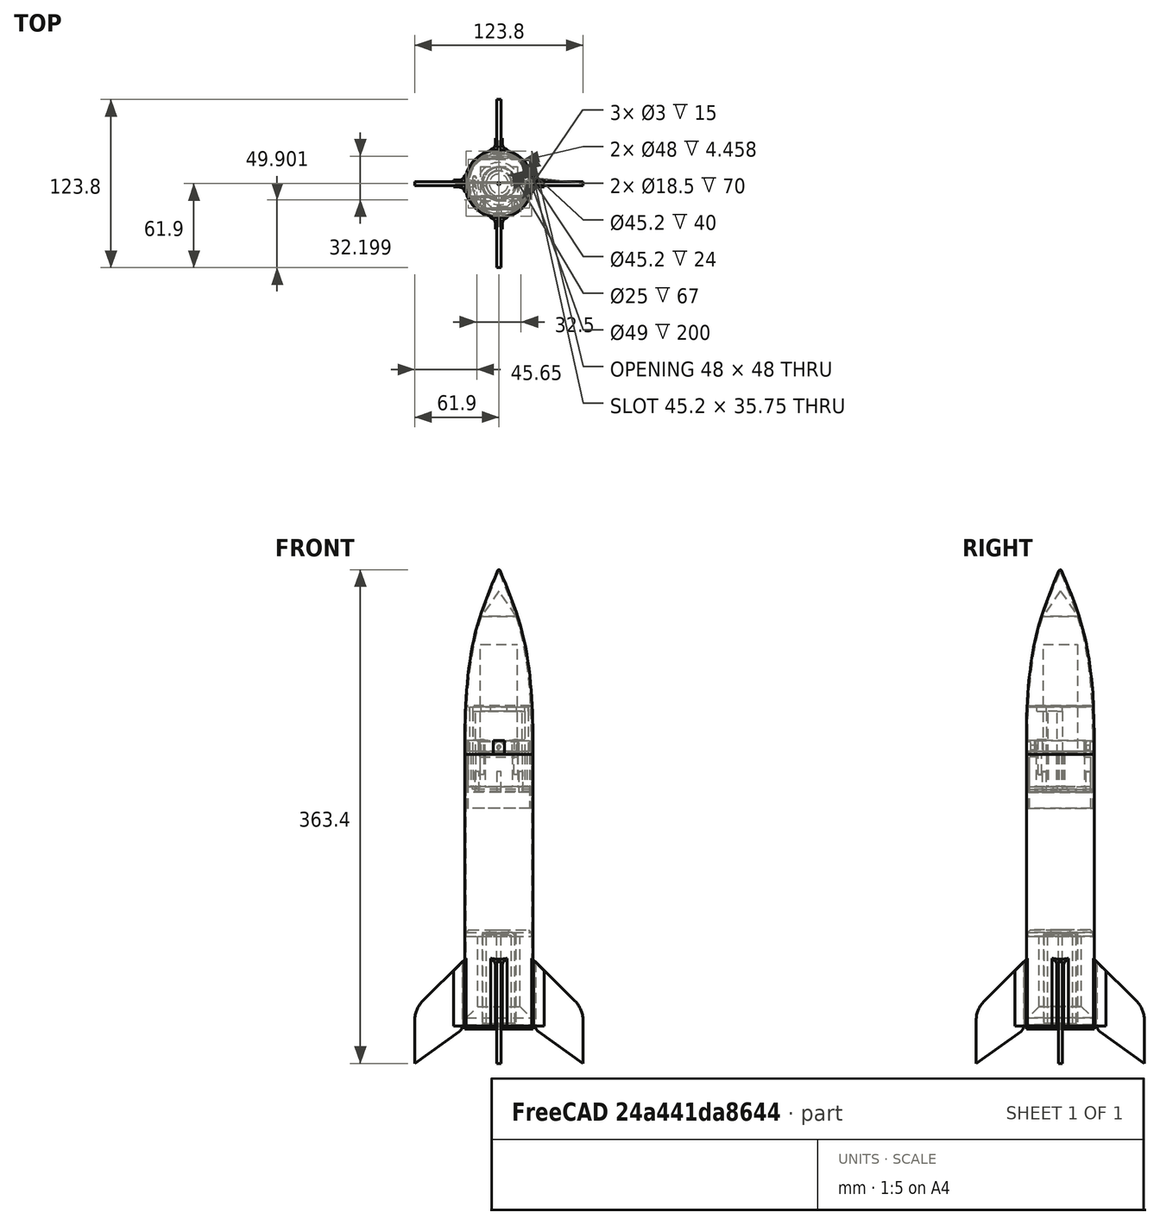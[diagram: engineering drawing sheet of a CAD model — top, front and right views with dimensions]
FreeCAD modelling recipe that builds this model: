
FCSTD DOCUMENT  (FreeCAD 0.21R33694 (Git))
Label: LaMule_V1.2
License: All rights reserved
LicenseURL: http://en.wikipedia.org/wiki/All_rights_reserved
objects: Sketcher::SketchObject×52, PartDesign::Pad×29, PartDesign::Body×19, PartDesign::Pocket×19, PartDesign::Fillet×12, PartDesign::Chamfer×11, Mesh::Feature×5, PartDesign::Revolution×4, App::LinkGroup×2, PartDesign::Thickness×2, TechDraw::DrawSVGTemplate×1, TechDraw::DrawViewPart×1, TechDraw::DrawPage×1
note: 225 computed .brp shape members not serialized (recipe doc carries the construction recipe); baked Part::Feature solids carry a one-line shape summary decoded from their .brp

FEATURE [Sketcher::SketchObject] Sketch
  FullyConstrained = true
  MapMode = 5
  Placement = pos=(0,0,0) rot=(1,0,0;1.5708rad)
  Support = -> [XZ_Plane]
  sketch-geometry (12):
    g0: LineSegment StartX=24 StartY=0 StartZ=0 EndX=7 EndY=0 EndZ=0
    g1: LineSegment StartX=7 StartY=0 StartZ=0 EndX=7 EndY=3 EndZ=0
    g2: LineSegment StartX=7 StartY=3 StartZ=0 EndX=12.5 EndY=3 EndZ=0
    g3: LineSegment StartX=12.5 StartY=3 StartZ=0 EndX=12.5 EndY=73 EndZ=0
    g4: LineSegment StartX=12.5 StartY=73 StartZ=0 EndX=25 EndY=73 EndZ=0
    g5: LineSegment StartX=25 StartY=73 StartZ=0 EndX=25 EndY=71 EndZ=0
    g6: LineSegment StartX=25 StartY=71 StartZ=0 EndX=24 EndY=70 EndZ=0
    g7: LineSegment StartX=24 StartY=70 StartZ=0 EndX=24 EndY=65 EndZ=0
    g8: LineSegment StartX=24 StartY=65 StartZ=0 EndX=15.5 EndY=56.5 EndZ=0
    g9: LineSegment StartX=15.5 StartY=56.5 StartZ=0 EndX=15.5 EndY=5 EndZ=0
    g10: LineSegment StartX=15.5 StartY=5 StartZ=0 EndX=24 EndY=5 EndZ=0
    g11: LineSegment StartX=24 StartY=5 StartZ=0 EndX=24 EndY=0 EndZ=0
  constraints (36):
    c: PointOnObject(g0,g-1)
    c: PointOnObject(g0,g-1)
    c: Coincident(g0,g1)
    c: Vertical(g1)
    c: Coincident(g1,g2)
    c: Horizontal(g2)
    c: Coincident(g2,g3)
    c: Vertical(g3)
    c: Coincident(g3,g4)
    c: Horizontal(g4)
    c: Coincident(g4,g5)
    c: Coincident(g5,g6)
    c: Coincident(g6,g7)
    c: Vertical(g7)
    c: Coincident(g7,g8)
    c: Coincident(g8,g9)
    c: Vertical(g9)
    c: Coincident(g9,g10)
    c: Horizontal(g10)
    c: Coincident(g10,g11)
    c: Coincident(g11,g0)
    c: DistanceX(g-2,g2) = 12.5
    c: DistanceY(g3,g3) = 70
    c: DistanceY(g1,g1) = 3
    c: DistanceX(g-2,g4) = 25
    c: Vertical(g5)
    c: DistanceY(g5,g5) = 2
    c: DistanceY(g7,g7) = 5
    c: DistanceX(g-1,g0) = 24
    c: DistanceX(g-2,g7) = 24
    c: Distance(g9,g3) = 3
    c: DistanceY(g11,g11) = 5
    c: Angle(g9,g8) = 2.35619
    c: Angle(g7,g6) = 2.35619
    c: Vertical(g11)
    c: DistanceX(g-2,g0) = 7
FEATURE [PartDesign::Revolution] Revolution
  Angle = 360
  Axis = (0,2e-16,1)
  Base = (0,0,0)
  Placement = pos=(0,0,0) rot=(1,0,0;1.5708rad)
  Profile = -> Sketch
  ReferenceAxis = -> Sketch [V_Axis]
  Reversed = true
FEATURE [PartDesign::Chamfer] Chamfer
  Angle = 45
  Base = -> Revolution [Edge6]
  BaseFeature = -> Revolution
  ChamferType = 0
  FlipDirection = false
  Placement = pos=(0,0,0) rot=(1,0,0;1.5708rad)
  Size = 3
  Size2 = 1
  SupportTransform = false
  UseAllEdges = false
FEATURE [PartDesign::Chamfer] Chamfer001
  Angle = 45
  Base = -> Chamfer [Edge12]
  BaseFeature = -> Chamfer
  ChamferType = 0
  FlipDirection = false
  Placement = pos=(0,0,0) rot=(1,0,0;1.5708rad)
  Size = 2
  Size2 = 1
  SupportTransform = false
  UseAllEdges = false
FEATURE [PartDesign::Body] Body  label="support_moteur_V1"
  Group = -> [Sketch,Revolution,Chamfer,Chamfer001]
  Origin = -> Origin
  Placement = pos=(7e-15,0,71) rot=(0,1,0;3.14159rad)
  Tip = -> Chamfer001
FEATURE [Sketcher::SketchObject] Sketch001
  FullyConstrained = true
  MapMode = 5
  Support = -> [XY_Plane001]
  sketch-geometry (2):
    g0: Circle CenterX=0 CenterY=0 CenterZ=0 NormalX=0 NormalY=0 NormalZ=1 AngleXU=0 Radius=24.5
    g1: Circle CenterX=0 CenterY=0 CenterZ=0 NormalX=0 NormalY=0 NormalZ=1 AngleXU=0 Radius=25
  constraints (4):
    c: Radius(g0) = 24.5
    c: Radius(g1) = 25
    c: Coincident(g0,g-1)
    c: Coincident(g1,g0)
FEATURE [PartDesign::Pad] Pad
  Direction = (1,1,1)
  Length = 200
  Length2 = 100
  Profile = -> Sketch001
  Type = 0
FEATURE [PartDesign::Body] Body001  label="tube_V1"
  Group = -> [Sketch001,Pad]
  Origin = -> Origin001
  Tip = -> Pad
FEATURE [Sketcher::SketchObject] Sketch002
  FullyConstrained = true
  MapMode = 5
  Support = -> [XY_Plane002]
  sketch-geometry (12):
    g0: ArcOfCircle CenterX=0 CenterY=0 CenterZ=0 NormalX=0 NormalY=0 NormalZ=1 AngleXU=0 Radius=25 StartAngle=6.04082 EndAngle=6.52555
    g1: LineSegment StartX=24.2693 StartY=-6 StartZ=0 EndX=25.2982 EndY=-6 EndZ=0
    g2: LineSegment StartX=24.2693 StartY=6 StartZ=0 EndX=25.2982 EndY=6 EndZ=0
    g3: LineSegment StartX=25.8697 StartY=2.6 StartZ=0 EndX=33.4517 EndY=2.6 EndZ=0
    g4: LineSegment StartX=33.4517 StartY=2.6 StartZ=0 EndX=33.4517 EndY=1.6 EndZ=0
    g5: LineSegment StartX=33.4517 StartY=1.6 StartZ=0 EndX=26.4517 EndY=1.6 EndZ=0
    g6: LineSegment StartX=26.4517 StartY=1.6 StartZ=0 EndX=26.4517 EndY=-1.6 EndZ=0
    g7: LineSegment StartX=26.4517 StartY=-1.6 StartZ=0 EndX=33.4517 EndY=-1.6 EndZ=0
    g8: LineSegment StartX=33.4517 StartY=-1.6 StartZ=0 EndX=33.4517 EndY=-2.6 EndZ=0
    g9: LineSegment StartX=33.4517 StartY=-2.6 StartZ=0 EndX=25.8697 EndY=-2.6 EndZ=0
    g10: ArcOfCircle CenterX=0 CenterY=0 CenterZ=0 NormalX=0 NormalY=0 NormalZ=1 AngleXU=0 Radius=26 StartAngle=6.05032 EndAngle=6.18302
    g11: ArcOfCircle CenterX=0 CenterY=0 CenterZ=0 NormalX=0 NormalY=0 NormalZ=1 AngleXU=0 Radius=26 StartAngle=0.100167 EndAngle=0.232868
  constraints (33):
    c: Coincident(g0,g-1)
    c: Radius(g0) = 25
    c: Coincident(g0,g1)
    c: Coincident(g0,g2)
    c: Horizontal(g3)
    c: Coincident(g3,g4)
    c: Coincident(g4,g5)
    c: Horizontal(g5)
    c: Coincident(g5,g6)
    c: Coincident(g6,g7)
    c: Horizontal(g7)
    c: Coincident(g7,g8)
    c: Coincident(g8,g9)
    c: Horizontal(g9)
    c: Coincident(g10,g0)
    c: Coincident(g10,g1)
    c: Coincident(g10,g9)
    c: Coincident(g11,g0)
    c: Coincident(g11,g2)
    c: Coincident(g11,g3)
    c: Radius(g11) = 26
    c: Horizontal(g2)
    c: Horizontal(g1)
    c: Symmetric(g7,g4,g-1)
    c: Vertical(g8)
    c: Vertical(g6)
    c: Distance(g6,g5) = 3.2
    c: DistanceY(g4,g4) = 1
    c: Distance(g5,g0) = 26.5
    c: Symmetric(g3,g8,g-1)
    c: DistanceX(g5,g5) = 7
    c: Symmetric(g2,g1,g-1)
    c: DistanceY(g-1,g2) = 6
FEATURE [PartDesign::Pad] Pad001
  Direction = (1,1,1)
  Length = 50
  Length2 = 100
  Profile = -> Sketch002
  Type = 0
FEATURE [PartDesign::Fillet] Fillet
  Base = -> Pad001 [Edge20,Edge1]
  BaseFeature = -> Pad001
  Radius = 4
  SupportTransform = false
  UseAllEdges = false
FEATURE [Sketcher::SketchObject] Sketch003
  ExternalGeometry = -> [Fillet]
  FullyConstrained = true
  MapMode = 5
  Placement = pos=(0,-2.6,0) rot=(1,0,0;1.5708rad)
  Support = -> [Fillet]
  sketch-geometry (3):
    g0: LineSegment StartX=33.4517 StartY=50 StartZ=0 EndX=33.4517 EndY=40.8177 EndZ=0
    g1: LineSegment StartX=33.4517 StartY=40.8177 StartZ=0 EndX=24.2693 EndY=50 EndZ=0
    g2: LineSegment StartX=24.2693 StartY=50 StartZ=0 EndX=33.4517 EndY=50 EndZ=0
  constraints (8):
    c: Coincident(g-4,g0)
    c: PointOnObject(g0,g-4)
    c: Coincident(g0,g1)
    c: PointOnObject(g1,g-3)
    c: Coincident(g1,g2)
    c: Coincident(g2,g0)
    c: Horizontal(g2)
    c: Angle(g1,g2) = 0.785398
FEATURE [PartDesign::Pocket] Pocket
  BaseFeature = -> Fillet
  Direction = (1,1,1)
  Length = 23
  Length2 = 100
  Midplane = true
  Profile = -> Sketch003
  Type = 1
FEATURE [PartDesign::Body] Body002  label="support_aileron_V1"
  Group = -> [Sketch002,Pad001,Fillet,Sketch003,Pocket]
  Origin = -> Origin002
  Tip = -> Pocket
FEATURE [Sketcher::SketchObject] Sketch004
  FullyConstrained = true
  MapMode = 5
  Support = -> [XY_Plane003]
  sketch-geometry (12):
    g0: ArcOfCircle CenterX=0 CenterY=0 CenterZ=0 NormalX=0 NormalY=0 NormalZ=1 AngleXU=0 Radius=25 StartAngle=6.04082 EndAngle=6.52555
    g1: LineSegment StartX=24.2693 StartY=-6 StartZ=0 EndX=25.2982 EndY=-6 EndZ=0
    g2: LineSegment StartX=24.2693 StartY=6 StartZ=0 EndX=25.2982 EndY=6 EndZ=0
    g3: LineSegment StartX=25.8697 StartY=2.6 StartZ=0 EndX=33.4517 EndY=2.6 EndZ=0
    g4: LineSegment StartX=33.4517 StartY=2.6 StartZ=0 EndX=33.4517 EndY=1.6 EndZ=0
    g5: LineSegment StartX=33.4517 StartY=1.6 StartZ=0 EndX=26.4517 EndY=1.6 EndZ=0
    g6: LineSegment StartX=26.4517 StartY=1.6 StartZ=0 EndX=26.4517 EndY=-1.6 EndZ=0
    g7: LineSegment StartX=26.4517 StartY=-1.6 StartZ=0 EndX=33.4517 EndY=-1.6 EndZ=0
    g8: LineSegment StartX=33.4517 StartY=-1.6 StartZ=0 EndX=33.4517 EndY=-2.6 EndZ=0
    g9: LineSegment StartX=33.4517 StartY=-2.6 StartZ=0 EndX=25.8697 EndY=-2.6 EndZ=0
    g10: ArcOfCircle CenterX=0 CenterY=0 CenterZ=0 NormalX=0 NormalY=0 NormalZ=1 AngleXU=0 Radius=26 StartAngle=6.05032 EndAngle=6.18302
    g11: ArcOfCircle CenterX=0 CenterY=0 CenterZ=0 NormalX=0 NormalY=0 NormalZ=1 AngleXU=0 Radius=26 StartAngle=0.100167 EndAngle=0.232868
  constraints (33):
    c: Coincident(g0,g-1)
    c: Radius(g0) = 25
    c: Coincident(g0,g1)
    c: Coincident(g0,g2)
    c: Horizontal(g3)
    c: Coincident(g3,g4)
    c: Coincident(g4,g5)
    c: Horizontal(g5)
    c: Coincident(g5,g6)
    c: Coincident(g6,g7)
    c: Horizontal(g7)
    c: Coincident(g7,g8)
    c: Coincident(g8,g9)
    c: Horizontal(g9)
    c: Coincident(g10,g0)
    c: Coincident(g10,g1)
    c: Coincident(g10,g9)
    c: Coincident(g11,g0)
    c: Coincident(g11,g2)
    c: Coincident(g11,g3)
    c: Radius(g11) = 26
    c: Horizontal(g2)
    c: Horizontal(g1)
    c: Symmetric(g7,g4,g-1)
    c: Vertical(g8)
    c: Vertical(g6)
    c: Distance(g6,g5) = 3.2
    c: DistanceY(g4,g4) = 1
    c: Distance(g5,g0) = 26.5
    c: Symmetric(g3,g8,g-1)
    c: DistanceX(g5,g5) = 7
    c: Symmetric(g2,g1,g-1)
    c: DistanceY(g-1,g2) = 6
FEATURE [PartDesign::Pad] Pad002
  Direction = (1,1,1)
  Length = 50
  Length2 = 100
  Profile = -> Sketch004
  Type = 0
FEATURE [PartDesign::Fillet] Fillet001
  Base = -> Pad002 [Edge20,Edge1]
  BaseFeature = -> Pad002
  Radius = 4
  SupportTransform = false
  UseAllEdges = false
FEATURE [Sketcher::SketchObject] Sketch005
  ExternalGeometry = -> [Fillet001]
  FullyConstrained = true
  MapMode = 5
  Placement = pos=(0,-2.6,0) rot=(1,0,0;1.5708rad)
  Support = -> [Fillet001]
  sketch-geometry (3):
    g0: LineSegment StartX=33.4517 StartY=50 StartZ=0 EndX=33.4517 EndY=40.8177 EndZ=0
    g1: LineSegment StartX=33.4517 StartY=40.8177 StartZ=0 EndX=24.2693 EndY=50 EndZ=0
    g2: LineSegment StartX=24.2693 StartY=50 StartZ=0 EndX=33.4517 EndY=50 EndZ=0
  constraints (8):
    c: Coincident(g-4,g0)
    c: PointOnObject(g0,g-4)
    c: Coincident(g0,g1)
    c: PointOnObject(g1,g-3)
    c: Coincident(g1,g2)
    c: Coincident(g2,g0)
    c: Horizontal(g2)
    c: Angle(g1,g2) = 0.785398
FEATURE [PartDesign::Pocket] Pocket001
  BaseFeature = -> Fillet001
  Direction = (1,1,1)
  Length = 23
  Length2 = 100
  Midplane = true
  Profile = -> Sketch005
  Type = 1
FEATURE [PartDesign::Body] Body003  label="support_aileron_V002"
  Group = -> [Sketch004,Pad002,Fillet001,Sketch005,Pocket001]
  Origin = -> Origin003
  Placement = pos=(0,0,0) rot=(0,0,1;1.5708rad)
  Tip = -> Pocket001
FEATURE [Sketcher::SketchObject] Sketch006
  FullyConstrained = true
  MapMode = 5
  Support = -> [XY_Plane004]
  sketch-geometry (12):
    g0: ArcOfCircle CenterX=0 CenterY=0 CenterZ=0 NormalX=0 NormalY=0 NormalZ=1 AngleXU=0 Radius=25 StartAngle=6.04082 EndAngle=6.52555
    g1: LineSegment StartX=24.2693 StartY=-6 StartZ=0 EndX=25.2982 EndY=-6 EndZ=0
    g2: LineSegment StartX=24.2693 StartY=6 StartZ=0 EndX=25.2982 EndY=6 EndZ=0
    g3: LineSegment StartX=25.8697 StartY=2.6 StartZ=0 EndX=33.4517 EndY=2.6 EndZ=0
    g4: LineSegment StartX=33.4517 StartY=2.6 StartZ=0 EndX=33.4517 EndY=1.6 EndZ=0
    g5: LineSegment StartX=33.4517 StartY=1.6 StartZ=0 EndX=26.4517 EndY=1.6 EndZ=0
    g6: LineSegment StartX=26.4517 StartY=1.6 StartZ=0 EndX=26.4517 EndY=-1.6 EndZ=0
    g7: LineSegment StartX=26.4517 StartY=-1.6 StartZ=0 EndX=33.4517 EndY=-1.6 EndZ=0
    g8: LineSegment StartX=33.4517 StartY=-1.6 StartZ=0 EndX=33.4517 EndY=-2.6 EndZ=0
    g9: LineSegment StartX=33.4517 StartY=-2.6 StartZ=0 EndX=25.8697 EndY=-2.6 EndZ=0
    g10: ArcOfCircle CenterX=0 CenterY=0 CenterZ=0 NormalX=0 NormalY=0 NormalZ=1 AngleXU=0 Radius=26 StartAngle=6.05032 EndAngle=6.18302
    g11: ArcOfCircle CenterX=0 CenterY=0 CenterZ=0 NormalX=0 NormalY=0 NormalZ=1 AngleXU=0 Radius=26 StartAngle=0.100167 EndAngle=0.232868
  constraints (33):
    c: Coincident(g0,g-1)
    c: Radius(g0) = 25
    c: Coincident(g0,g1)
    c: Coincident(g0,g2)
    c: Horizontal(g3)
    c: Coincident(g3,g4)
    c: Coincident(g4,g5)
    c: Horizontal(g5)
    c: Coincident(g5,g6)
    c: Coincident(g6,g7)
    c: Horizontal(g7)
    c: Coincident(g7,g8)
    c: Coincident(g8,g9)
    c: Horizontal(g9)
    c: Coincident(g10,g0)
    c: Coincident(g10,g1)
    c: Coincident(g10,g9)
    c: Coincident(g11,g0)
    c: Coincident(g11,g2)
    c: Coincident(g11,g3)
    c: Radius(g11) = 26
    c: Horizontal(g2)
    c: Horizontal(g1)
    c: Symmetric(g7,g4,g-1)
    c: Vertical(g8)
    c: Vertical(g6)
    c: Distance(g6,g5) = 3.2
    c: DistanceY(g4,g4) = 1
    c: Distance(g5,g0) = 26.5
    c: Symmetric(g3,g8,g-1)
    c: DistanceX(g5,g5) = 7
    c: Symmetric(g2,g1,g-1)
    c: DistanceY(g-1,g2) = 6
FEATURE [PartDesign::Pad] Pad003
  Direction = (1,1,1)
  Length = 50
  Length2 = 100
  Profile = -> Sketch006
  Type = 0
FEATURE [PartDesign::Fillet] Fillet002
  Base = -> Pad003 [Edge20,Edge1]
  BaseFeature = -> Pad003
  Radius = 4
  SupportTransform = false
  UseAllEdges = false
FEATURE [Sketcher::SketchObject] Sketch007
  ExternalGeometry = -> [Fillet002]
  FullyConstrained = true
  MapMode = 5
  Placement = pos=(0,-2.6,0) rot=(1,0,0;1.5708rad)
  Support = -> [Fillet002]
  sketch-geometry (3):
    g0: LineSegment StartX=33.4517 StartY=50 StartZ=0 EndX=33.4517 EndY=40.8177 EndZ=0
    g1: LineSegment StartX=33.4517 StartY=40.8177 StartZ=0 EndX=24.2693 EndY=50 EndZ=0
    g2: LineSegment StartX=24.2693 StartY=50 StartZ=0 EndX=33.4517 EndY=50 EndZ=0
  constraints (8):
    c: Coincident(g-4,g0)
    c: PointOnObject(g0,g-4)
    c: Coincident(g0,g1)
    c: PointOnObject(g1,g-3)
    c: Coincident(g1,g2)
    c: Coincident(g2,g0)
    c: Horizontal(g2)
    c: Angle(g1,g2) = 0.785398
FEATURE [PartDesign::Pocket] Pocket002
  BaseFeature = -> Fillet002
  Direction = (1,1,1)
  Length = 23
  Length2 = 100
  Midplane = true
  Profile = -> Sketch007
  Type = 1
FEATURE [PartDesign::Body] Body004  label="support_aileron_V003"
  Group = -> [Sketch006,Pad003,Fillet002,Sketch007,Pocket002]
  Origin = -> Origin004
  Placement = pos=(0,0,0) rot=(0,0,1;3.14159rad)
  Tip = -> Pocket002
FEATURE [Sketcher::SketchObject] Sketch008
  FullyConstrained = true
  MapMode = 5
  Support = -> [XY_Plane005]
  sketch-geometry (12):
    g0: ArcOfCircle CenterX=0 CenterY=0 CenterZ=0 NormalX=0 NormalY=0 NormalZ=1 AngleXU=0 Radius=25 StartAngle=6.04082 EndAngle=6.52555
    g1: LineSegment StartX=24.2693 StartY=-6 StartZ=0 EndX=25.2982 EndY=-6 EndZ=0
    g2: LineSegment StartX=24.2693 StartY=6 StartZ=0 EndX=25.2982 EndY=6 EndZ=0
    g3: LineSegment StartX=25.8697 StartY=2.6 StartZ=0 EndX=33.4517 EndY=2.6 EndZ=0
    g4: LineSegment StartX=33.4517 StartY=2.6 StartZ=0 EndX=33.4517 EndY=1.6 EndZ=0
    g5: LineSegment StartX=33.4517 StartY=1.6 StartZ=0 EndX=26.4517 EndY=1.6 EndZ=0
    g6: LineSegment StartX=26.4517 StartY=1.6 StartZ=0 EndX=26.4517 EndY=-1.6 EndZ=0
    g7: LineSegment StartX=26.4517 StartY=-1.6 StartZ=0 EndX=33.4517 EndY=-1.6 EndZ=0
    g8: LineSegment StartX=33.4517 StartY=-1.6 StartZ=0 EndX=33.4517 EndY=-2.6 EndZ=0
    g9: LineSegment StartX=33.4517 StartY=-2.6 StartZ=0 EndX=25.8697 EndY=-2.6 EndZ=0
    g10: ArcOfCircle CenterX=0 CenterY=0 CenterZ=0 NormalX=0 NormalY=0 NormalZ=1 AngleXU=0 Radius=26 StartAngle=6.05032 EndAngle=6.18302
    g11: ArcOfCircle CenterX=0 CenterY=0 CenterZ=0 NormalX=0 NormalY=0 NormalZ=1 AngleXU=0 Radius=26 StartAngle=0.100167 EndAngle=0.232868
  constraints (33):
    c: Coincident(g0,g-1)
    c: Radius(g0) = 25
    c: Coincident(g0,g1)
    c: Coincident(g0,g2)
    c: Horizontal(g3)
    c: Coincident(g3,g4)
    c: Coincident(g4,g5)
    c: Horizontal(g5)
    c: Coincident(g5,g6)
    c: Coincident(g6,g7)
    c: Horizontal(g7)
    c: Coincident(g7,g8)
    c: Coincident(g8,g9)
    c: Horizontal(g9)
    c: Coincident(g10,g0)
    c: Coincident(g10,g1)
    c: Coincident(g10,g9)
    c: Coincident(g11,g0)
    c: Coincident(g11,g2)
    c: Coincident(g11,g3)
    c: Radius(g11) = 26
    c: Horizontal(g2)
    c: Horizontal(g1)
    c: Symmetric(g7,g4,g-1)
    c: Vertical(g8)
    c: Vertical(g6)
    c: Distance(g6,g5) = 3.2
    c: DistanceY(g4,g4) = 1
    c: Distance(g5,g0) = 26.5
    c: Symmetric(g3,g8,g-1)
    c: DistanceX(g5,g5) = 7
    c: Symmetric(g2,g1,g-1)
    c: DistanceY(g-1,g2) = 6
FEATURE [PartDesign::Pad] Pad004
  Direction = (1,1,1)
  Length = 50
  Length2 = 100
  Profile = -> Sketch008
  Type = 0
FEATURE [PartDesign::Fillet] Fillet003
  Base = -> Pad004 [Edge20,Edge1]
  BaseFeature = -> Pad004
  Radius = 4
  SupportTransform = false
  UseAllEdges = false
FEATURE [Sketcher::SketchObject] Sketch009
  ExternalGeometry = -> [Fillet003]
  FullyConstrained = true
  MapMode = 5
  Placement = pos=(0,-2.6,0) rot=(1,0,0;1.5708rad)
  Support = -> [Fillet003]
  sketch-geometry (3):
    g0: LineSegment StartX=33.4517 StartY=50 StartZ=0 EndX=33.4517 EndY=40.8177 EndZ=0
    g1: LineSegment StartX=33.4517 StartY=40.8177 StartZ=0 EndX=24.2693 EndY=50 EndZ=0
    g2: LineSegment StartX=24.2693 StartY=50 StartZ=0 EndX=33.4517 EndY=50 EndZ=0
  constraints (8):
    c: Coincident(g-4,g0)
    c: PointOnObject(g0,g-4)
    c: Coincident(g0,g1)
    c: PointOnObject(g1,g-3)
    c: Coincident(g1,g2)
    c: Coincident(g2,g0)
    c: Horizontal(g2)
    c: Angle(g1,g2) = 0.785398
FEATURE [PartDesign::Pocket] Pocket003
  BaseFeature = -> Fillet003
  Direction = (1,1,1)
  Length = 23
  Length2 = 100
  Midplane = true
  Profile = -> Sketch009
  Type = 1
FEATURE [PartDesign::Body] Body005  label="support_aileron_V004"
  Group = -> [Sketch008,Pad004,Fillet003,Sketch009,Pocket003]
  Origin = -> Origin005
  Placement = pos=(0,0,0) rot=(0,0,-1;1.5708rad)
  Tip = -> Pocket003
FEATURE [App::LinkGroup] LinkGroup  label="support_ailerons_V1"
  ElementList = -> [Body005,Body004,Body003,Body002]
  LinkMode = 0
FEATURE [Sketcher::SketchObject] Sketch010
  FullyConstrained = true
  MapMode = 5
  Placement = pos=(0,0,0) rot=(0.57735,0.57735,0.57735;2.0944rad)
  Support = -> [YZ_Plane006]
  sketch-geometry (4):
    g0: LineSegment StartX=27 StartY=-2.5 StartZ=0 EndX=61.9 EndY=-27.4 EndZ=0
    g1: LineSegment StartX=61.9 StartY=-27.4 StartZ=0 EndX=61.9 EndY=12.6 EndZ=0
    g2: LineSegment StartX=61.9 StartY=12.6 StartZ=0 EndX=27 EndY=47.5 EndZ=0
    g3: LineSegment StartX=27 StartY=47.5 StartZ=0 EndX=27 EndY=-2.5 EndZ=0
  constraints (12):
    c: Coincident(g0,g1)
    c: Vertical(g1)
    c: Coincident(g1,g2)
    c: Coincident(g2,g3)
    c: Coincident(g3,g0)
    c: Vertical(g3)
    c: DistanceY(g3,g3) = 50
    c: DistanceY(g-1,g2) = 47.5
    c: DistanceX(g-2,g0) = 27
    c: Angle(g3,g2) = 0.785398
    c: DistanceY(g1,g1) = 40
    c: DistanceX(g-2,g0) = 61.9
FEATURE [PartDesign::Pad] Pad005
  Direction = (1,1,1)
  Length = 3
  Length2 = 100
  Midplane = true
  Placement = pos=(0,0,0) rot=(0.57735,0.57735,0.57735;2.0944rad)
  Profile = -> Sketch010
  Type = 0
FEATURE [PartDesign::Fillet] Fillet004
  Base = -> Pad005 [Edge5]
  BaseFeature = -> Pad005
  Placement = pos=(0,0,0) rot=(0.57735,0.57735,0.57735;2.0944rad)
  Radius = 20
  SupportTransform = false
  UseAllEdges = false
FEATURE [PartDesign::Fillet] Fillet005
  Base = -> Fillet004 [Edge11]
  BaseFeature = -> Fillet004
  Placement = pos=(0,0,0) rot=(0.57735,0.57735,0.57735;2.0944rad)
  Radius = 5
  SupportTransform = false
  UseAllEdges = false
FEATURE [PartDesign::Body] Body006  label="ailerons_V1"
  Group = -> [Sketch010,Pad005,Fillet004,Fillet005]
  Origin = -> Origin006
  Tip = -> Fillet005
FEATURE [Sketcher::SketchObject] Sketch011
  FullyConstrained = true
  MapMode = 5
  Placement = pos=(0,0,0) rot=(0.57735,0.57735,0.57735;2.0944rad)
  Support = -> [YZ_Plane007]
  sketch-geometry (4):
    g0: LineSegment StartX=27 StartY=-2.5 StartZ=0 EndX=61.9 EndY=-27.4 EndZ=0
    g1: LineSegment StartX=61.9 StartY=-27.4 StartZ=0 EndX=61.9 EndY=12.6 EndZ=0
    g2: LineSegment StartX=61.9 StartY=12.6 StartZ=0 EndX=27 EndY=47.5 EndZ=0
    g3: LineSegment StartX=27 StartY=47.5 StartZ=0 EndX=27 EndY=-2.5 EndZ=0
  constraints (12):
    c: Coincident(g0,g1)
    c: Vertical(g1)
    c: Coincident(g1,g2)
    c: Coincident(g2,g3)
    c: Coincident(g3,g0)
    c: Vertical(g3)
    c: DistanceY(g3,g3) = 50
    c: DistanceY(g-1,g2) = 47.5
    c: DistanceX(g-2,g0) = 27
    c: Angle(g3,g2) = 0.785398
    c: DistanceY(g1,g1) = 40
    c: DistanceX(g-2,g0) = 61.9
FEATURE [PartDesign::Pad] Pad006
  Direction = (1,1,1)
  Length = 3
  Length2 = 100
  Midplane = true
  Placement = pos=(0,0,0) rot=(0.57735,0.57735,0.57735;2.0944rad)
  Profile = -> Sketch011
  Type = 0
FEATURE [PartDesign::Fillet] Fillet006
  Base = -> Pad006 [Edge5]
  BaseFeature = -> Pad006
  Placement = pos=(0,0,0) rot=(0.57735,0.57735,0.57735;2.0944rad)
  Radius = 20
  SupportTransform = false
  UseAllEdges = false
FEATURE [PartDesign::Fillet] Fillet007
  Base = -> Fillet006 [Edge11]
  BaseFeature = -> Fillet006
  Placement = pos=(0,0,0) rot=(0.57735,0.57735,0.57735;2.0944rad)
  Radius = 5
  SupportTransform = false
  UseAllEdges = false
FEATURE [PartDesign::Body] Body007  label="ailerons_V002"
  Group = -> [Sketch011,Pad006,Fillet006,Fillet007]
  Origin = -> Origin007
  Placement = pos=(0,0,0) rot=(0,0,1;3.14159rad)
  Tip = -> Fillet007
FEATURE [Sketcher::SketchObject] Sketch012
  FullyConstrained = true
  MapMode = 5
  Placement = pos=(0,0,0) rot=(0.57735,0.57735,0.57735;2.0944rad)
  Support = -> [YZ_Plane008]
  sketch-geometry (4):
    g0: LineSegment StartX=27 StartY=-2.5 StartZ=0 EndX=61.9 EndY=-27.4 EndZ=0
    g1: LineSegment StartX=61.9 StartY=-27.4 StartZ=0 EndX=61.9 EndY=12.6 EndZ=0
    g2: LineSegment StartX=61.9 StartY=12.6 StartZ=0 EndX=27 EndY=47.5 EndZ=0
    g3: LineSegment StartX=27 StartY=47.5 StartZ=0 EndX=27 EndY=-2.5 EndZ=0
  constraints (12):
    c: Coincident(g0,g1)
    c: Vertical(g1)
    c: Coincident(g1,g2)
    c: Coincident(g2,g3)
    c: Coincident(g3,g0)
    c: Vertical(g3)
    c: DistanceY(g3,g3) = 50
    c: DistanceY(g-1,g2) = 47.5
    c: DistanceX(g-2,g0) = 27
    c: Angle(g3,g2) = 0.785398
    c: DistanceY(g1,g1) = 40
    c: DistanceX(g-2,g0) = 61.9
FEATURE [PartDesign::Pad] Pad007
  Direction = (1,1,1)
  Length = 3
  Length2 = 100
  Midplane = true
  Placement = pos=(0,0,0) rot=(0.57735,0.57735,0.57735;2.0944rad)
  Profile = -> Sketch012
  Type = 0
FEATURE [PartDesign::Fillet] Fillet008
  Base = -> Pad007 [Edge5]
  BaseFeature = -> Pad007
  Placement = pos=(0,0,0) rot=(0.57735,0.57735,0.57735;2.0944rad)
  Radius = 20
  SupportTransform = false
  UseAllEdges = false
FEATURE [PartDesign::Fillet] Fillet009
  Base = -> Fillet008 [Edge11]
  BaseFeature = -> Fillet008
  Placement = pos=(0,0,0) rot=(0.57735,0.57735,0.57735;2.0944rad)
  Radius = 5
  SupportTransform = false
  UseAllEdges = false
FEATURE [PartDesign::Body] Body008  label="ailerons_V003"
  Group = -> [Sketch012,Pad007,Fillet008,Fillet009]
  Origin = -> Origin008
  Placement = pos=(0,0,0) rot=(0,0,1;1.5708rad)
  Tip = -> Fillet009
FEATURE [Sketcher::SketchObject] Sketch013
  FullyConstrained = true
  MapMode = 5
  Placement = pos=(0,0,0) rot=(0.57735,0.57735,0.57735;2.0944rad)
  Support = -> [YZ_Plane009]
  sketch-geometry (4):
    g0: LineSegment StartX=27 StartY=-2.5 StartZ=0 EndX=61.9 EndY=-27.4 EndZ=0
    g1: LineSegment StartX=61.9 StartY=-27.4 StartZ=0 EndX=61.9 EndY=12.6 EndZ=0
    g2: LineSegment StartX=61.9 StartY=12.6 StartZ=0 EndX=27 EndY=47.5 EndZ=0
    g3: LineSegment StartX=27 StartY=47.5 StartZ=0 EndX=27 EndY=-2.5 EndZ=0
  constraints (12):
    c: Coincident(g0,g1)
    c: Vertical(g1)
    c: Coincident(g1,g2)
    c: Coincident(g2,g3)
    c: Coincident(g3,g0)
    c: Vertical(g3)
    c: DistanceY(g3,g3) = 50
    c: DistanceY(g-1,g2) = 47.5
    c: DistanceX(g-2,g0) = 27
    c: Angle(g3,g2) = 0.785398
    c: DistanceY(g1,g1) = 40
    c: DistanceX(g-2,g0) = 61.9
FEATURE [PartDesign::Pad] Pad008
  Direction = (1,1,1)
  Length = 3
  Length2 = 100
  Midplane = true
  Placement = pos=(0,0,0) rot=(0.57735,0.57735,0.57735;2.0944rad)
  Profile = -> Sketch013
  Type = 0
FEATURE [PartDesign::Fillet] Fillet010
  Base = -> Pad008 [Edge5]
  BaseFeature = -> Pad008
  Placement = pos=(0,0,0) rot=(0.57735,0.57735,0.57735;2.0944rad)
  Radius = 20
  SupportTransform = false
  UseAllEdges = false
FEATURE [PartDesign::Fillet] Fillet011
  Base = -> Fillet010 [Edge11]
  BaseFeature = -> Fillet010
  Placement = pos=(0,0,0) rot=(0.57735,0.57735,0.57735;2.0944rad)
  Radius = 5
  SupportTransform = false
  UseAllEdges = false
FEATURE [PartDesign::Body] Body009  label="ailerons_V004"
  Group = -> [Sketch013,Pad008,Fillet010,Fillet011]
  Origin = -> Origin009
  Placement = pos=(0,0,0) rot=(0,0,-1;1.5708rad)
  Tip = -> Fillet011
FEATURE [App::LinkGroup] LinkGroup001  label="ailerons"
  ElementList = -> [Body009,Body008,Body007,Body006]
  LinkMode = 0
FEATURE [Sketcher::SketchObject] Sketch014
  FullyConstrained = true
  MapMode = 5
  Support = -> [XY_Plane010]
  sketch-geometry (12):
    g0: LineSegment StartX=0 StartY=0 StartZ=0 EndX=134.73 EndY=0 EndZ=0
    g1: LineSegment StartX=134.73 StartY=-24 StartZ=0 EndX=134.73 EndY=0 EndZ=0
    g2: LineSegment StartX=134.73 StartY=-24 StartZ=0 EndX=120.272 EndY=-24 EndZ=0
    g3-g7: Circle x5 (B-spline internal-alignment scaffolding for g8; pole/knot coordinates omitted)
    g8: BSplineCurve PolesCount=5 KnotsCount=3 Degree=3 IsPeriodic=0
    g9: GeomPoint X=120.272 Y=-24 Z=0
    g10: GeomPoint X=62.1183 Y=-19.6849 Z=0
    g11: GeomPoint X=0 Y=0 Z=0
  constraints (23):
    c: Coincident(g0,g-1)
    c: PointOnObject(g0,g-1)
    c: Coincident(g1,g0)
    c: Vertical(g1)
    c: Coincident(g2,g1)
    c: Horizontal(g2)
    c: Coincident(g8,g2)
    c: Weight(g3) = 1
    c: Equal(g3, g4-g7) x4
    c: Coincident(g8,g0)
    c: InternalAlignment(g3-g7 -> g8) x5
    c: InternalAlignment(g9,g8)
    c: InternalAlignment(g10,g8)
    c: InternalAlignment(g11,g8)
    c: DistanceX(g6) = 33.4091
    c: DistanceY(g6) = -14.1378
    c: DistanceX(g5) = 61.0359
    c: DistanceY(g5) = -20.426
    c: DistanceX(g4) = 92.9923
    c: DistanceY(g4) = -23.75
    c: DistanceX(g2) = 120.272
    c: DistanceY(g2) = -24
    c: DistanceX(g0,g0) = 134.73
FEATURE [PartDesign::Revolution] Revolution001
  Angle = 360
  Axis = (1,0,0)
  Base = (0,0,0)
  Profile = -> Sketch014
  ReferenceAxis = -> X_Axis010
  Reversed = true
FEATURE [PartDesign::Thickness] Thickness
  Base = -> Revolution001 [Face1]
  BaseFeature = -> Revolution001
  Intersection = false
  Join = 0
  Mode = 0
  SupportTransform = false
  Value = 1
FEATURE [Sketcher::SketchObject] Sketch015
  FullyConstrained = true
  MapMode = 5
  Placement = pos=(134.73,0,0) rot=(0.57735,0.57735,0.57735;2.0944rad)
  Support = -> [Thickness]
  sketch-geometry (5):
    g0: Circle CenterX=1.1e-15 CenterY=0 CenterZ=0 NormalX=0 NormalY=0 NormalZ=1 AngleXU=0 Radius=25
    g1: ArcOfCircle CenterX=1.1e-15 CenterY=0 CenterZ=0 NormalX=0 NormalY=0 NormalZ=1 AngleXU=0 Radius=24 StartAngle=0.675132 EndAngle=2.46646
    g2: ArcOfCircle CenterX=1.1e-15 CenterY=0 CenterZ=0 NormalX=0 NormalY=0 NormalZ=1 AngleXU=0 Radius=24 StartAngle=3.81672 EndAngle=5.60805
    g3: LineSegment StartX=-18.735 StartY=15 StartZ=0 EndX=-18.735 EndY=-15 EndZ=0
    g4: LineSegment StartX=18.735 StartY=15 StartZ=0 EndX=18.735 EndY=-15 EndZ=0
  constraints (14):
    c: Coincident(g0,g-1)
    c: Radius(g0) = 25
    c: Coincident(g1,g0)
    c: Coincident(g2,g0)
    c: Symmetric(g2,g2,g-2)
    c: Symmetric(g2,g1,g-1)
    c: Radius(g1) = 24
    c: Equal(g1,g2)
    c: Coincident(g3,g1)
    c: Coincident(g3,g2)
    c: Coincident(g4,g1)
    c: Coincident(g4,g2)
    c: Symmetric(g1,g1,g-2)
    c: DistanceY(g4,g4) = 30
FEATURE [PartDesign::Pad] Pad009
  BaseFeature = -> Thickness
  Direction = (1,1,1)
  Length = 10
  Length2 = 100
  Profile = -> Sketch015
  Reversed = true
  Type = 0
FEATURE [PartDesign::Chamfer] Chamfer002
  Angle = 45
  Base = -> Pad009 [Edge9,Edge6]
  BaseFeature = -> Pad009
  ChamferType = 0
  FlipDirection = false
  Size = 1
  Size2 = 1
  SupportTransform = false
  UseAllEdges = false
FEATURE [PartDesign::Body] Body010  label="coiffe_V1"
  Group = -> [Sketch014,Revolution001,Thickness,Sketch015,Pad009,Chamfer002]
  Origin = -> Origin010
  Placement = pos=(-7.4e-14,0,335) rot=(0,1,0;1.5708rad)
  Tip = -> Chamfer002
FEATURE [Mesh::Feature] Mesh  label="coiffe_V1 (Meshed)"
FEATURE [TechDraw::DrawSVGTemplate] Template
  EditableTexts = Approved1=N/A; Approved2=N/A; CheckedBy=Papas Inventeurs; Code=Code; CompanyAddress=planête Terre, système solaire; CompanyName=Lift Off; DrawingNumber=1; DrawingTitle1=LaMule; DrawingTitle2=Envoyons quelque chose en l'air!; DrawingTitle3="Just because"; DrawnBy=Maël & PéPé; Revision=Rev 1; Scale=Scale; Sheet=Page 1 de 1
  Height = 215.9
  Orientation = 1
  Width = 279.4
FEATURE [TechDraw::DrawViewPart] View001
  CoarseView = false
  Direction = (0.207,0.686,-0.698)
  Focus = 100
  HardHidden = false
  IsoCount = 0
  IsoHidden = false
  IsoVisible = false
  LockPosition = false
  Perspective = false
  Rotation = 0
  Scale = 0.7
  ScaleType = 2
  ScrubCount = 0
  SeamHidden = false
  SeamVisible = true
  SmoothHidden = false
  SmoothVisible = true
  Source = -> [Body,Body001,Body010]
  X = 146.884
  XDirection = (-0.176,0.728,0.663)
  XSource = -> [LinkGroup,LinkGroup001]
  Y = 131.376
FEATURE [TechDraw::DrawPage] Page
  KeepUpdated = true
  NextBalloonIndex = 1
  ProjectionType = 0
  Template = -> Template
  Views = -> [View001]
FEATURE [Sketcher::SketchObject] Sketch016
  FullyConstrained = true
  MapMode = 5
  Support = -> [XY_Plane011]
  sketch-geometry (8):
    g0: ArcOfCircle CenterX=0 CenterY=-2.3e-15 CenterZ=0 NormalX=0 NormalY=0 NormalZ=1 AngleXU=0 Radius=23.8 StartAngle=2.2259 EndAngle=4.05728
    g1: ArcOfCircle CenterX=0 CenterY=-2.3e-15 CenterZ=0 NormalX=0 NormalY=0 NormalZ=1 AngleXU=0 Radius=23.8 StartAngle=5.3675 EndAngle=7.19888
    g2: LineSegment StartX=-14.5 StartY=-18.873 StartZ=0 EndX=14.5 EndY=-18.873 EndZ=0
    g3: LineSegment StartX=-14.5 StartY=18.873 StartZ=0 EndX=14.5 EndY=18.873 EndZ=0
    g4: ArcOfCircle CenterX=0 CenterY=-2.3e-15 CenterZ=0 NormalX=0 NormalY=0 NormalZ=1 AngleXU=0 Radius=22.6 StartAngle=2.22941 EndAngle=4.05377
    g5: ArcOfCircle CenterX=0 CenterY=-2.3e-15 CenterZ=0 NormalX=0 NormalY=0 NormalZ=1 AngleXU=0 Radius=22.6 StartAngle=5.371 EndAngle=7.19537
    g6: LineSegment StartX=-13.8317 StartY=17.873 StartZ=0 EndX=13.8317 EndY=17.873 EndZ=0
    g7: LineSegment StartX=13.8317 StartY=-17.873 StartZ=0 EndX=-13.8317 EndY=-17.873 EndZ=0
  constraints (22):
    c: Coincident(g0,g-1)
    c: Coincident(g0,g1)
    c: Coincident(g0,g2)
    c: Coincident(g1,g2)
    c: Coincident(g1,g3)
    c: Coincident(g0,g3)
    c: Symmetric(g1,g0,g-2)
    c: Symmetric(g0,g1,g-2)
    c: Radius(g1) = 23.8
    c: Symmetric(g0,g0,g-1)
    c: DistanceX(g2,g2) = 29
    c: Coincident(g4,g0)
    c: Coincident(g5,g0)
    c: Coincident(g6,g4)
    c: Coincident(g6,g5)
    c: Coincident(g7,g5)
    c: Coincident(g7,g4)
    c: Symmetric(g5,g5,g-1)
    c: Symmetric(g5,g4,g-2)
    c: Radius(g5) = 22.6
    c: Horizontal(g7)
    c: Distance(g4,g3) = 1
FEATURE [PartDesign::Pad] Pad010
  Direction = (1,1,1)
  Length = 10
  Length2 = 100
  Profile = -> Sketch016
  Type = 0
FEATURE [PartDesign::Chamfer] Chamfer003
  Angle = 45
  Base = -> Pad010 [Edge7,Edge12]
  BaseFeature = -> Pad010
  ChamferType = 0
  FlipDirection = false
  Size = 0.5
  Size2 = 1
  SupportTransform = false
  UseAllEdges = false
FEATURE [Sketcher::SketchObject] Sketch017
  FullyConstrained = true
  MapMode = 5
  Placement = pos=(0,0,0) rot=(1,0,0;3.14159rad)
  Support = -> [Chamfer003]
  sketch-geometry (2):
    g0: Circle CenterX=0 CenterY=0 CenterZ=0 NormalX=0 NormalY=0 NormalZ=1 AngleXU=0 Radius=23.9
    g1: Circle CenterX=0 CenterY=0 CenterZ=0 NormalX=0 NormalY=0 NormalZ=1 AngleXU=0 Radius=22.6
  constraints (4):
    c: Coincident(g0,g-1)
    c: Radius(g0) = 23.9
    c: Coincident(g1,g0)
    c: Radius(g1) = 22.6
FEATURE [PartDesign::Pad] Pad011
  BaseFeature = -> Chamfer003
  Direction = (0,0,-1)
  Length = 40
  Length2 = 100
  Profile = -> Sketch017
  ReferenceAxis = -> Sketch017 [N_Axis]
  Type = 0
FEATURE [Sketcher::SketchObject] Sketch018
  ExternalGeometry = -> [Pad011]
  FullyConstrained = true
  MapMode = 5
  Placement = pos=(0,0,0) rot=(1,0,0;3.14159rad)
  Support = -> [Pad011]
  sketch-geometry (4):
    g0: ArcOfCircle CenterX=-1.1e-15 CenterY=0 CenterZ=0 NormalX=0 NormalY=0 NormalZ=1 AngleXU=0 Radius=23.9 StartAngle=3.98637 EndAngle=5.43841
    g1: ArcOfCircle CenterX=-1.1e-15 CenterY=0 CenterZ=0 NormalX=0 NormalY=0 NormalZ=1 AngleXU=0 Radius=23.9 StartAngle=0.844779 EndAngle=2.29681
    g2: LineSegment StartX=-15.8671 StartY=17.873 StartZ=0 EndX=15.8671 EndY=17.873 EndZ=0
    g3: LineSegment StartX=-15.8671 StartY=-17.873 StartZ=0 EndX=15.8671 EndY=-17.873 EndZ=0
  constraints (14):
    c: Coincident(g0,g-1)
    c: PointOnObject(g0,g-3)
    c: PointOnObject(g0,g-3)
    c: Coincident(g1,g0)
    c: PointOnObject(g1,g-3)
    c: PointOnObject(g1,g-3)
    c: Coincident(g2,g1)
    c: Coincident(g2,g1)
    c: Horizontal(g2)
    c: PointOnObject(g-4,g2)
    c: Coincident(g3,g0)
    c: Coincident(g3,g0)
    c: Horizontal(g3)
    c: PointOnObject(g-5,g3)
FEATURE [PartDesign::Pad] Pad012
  BaseFeature = -> Pad011
  Direction = (0,0,-1)
  Length = 2
  Length2 = 100
  Profile = -> Sketch018
  Type = 0
FEATURE [Sketcher::SketchObject] Sketch019
  ExternalGeometry = -> [Pad012]
  FullyConstrained = true
  MapMode = 5
  Support = -> [Pad012]
  sketch-geometry (3):
    g0: Circle CenterX=-18 CenterY=4 CenterZ=0 NormalX=0 NormalY=0 NormalZ=1 AngleXU=0 Radius=1.5
    g1: Circle CenterX=-18 CenterY=-4 CenterZ=0 NormalX=0 NormalY=0 NormalZ=1 AngleXU=0 Radius=1.5
    g2: Circle CenterX=0 CenterY=0 CenterZ=0 NormalX=0 NormalY=0 NormalZ=1 AngleXU=0 Radius=23.9
  constraints (7):
    c: Radius(g1) = 1.5
    c: Equal(g1,g0)
    c: Symmetric(g0,g1,g-1)
    c: DistanceX(g0) = -18
    c: DistanceY(g0) = 4
    c: Radius(g2) = 23.9
    c: Coincident(g2,g-1)
FEATURE [PartDesign::Pad] Pad013
  BaseFeature = -> Pad012
  Direction = (0,0,1)
  Length = 2
  Length2 = 100
  Profile = -> Sketch019
  Type = 0
FEATURE [PartDesign::Chamfer] Chamfer004
  Angle = 45
  Base = -> Pad013 [Edge42]
  BaseFeature = -> Pad013
  ChamferType = 0
  FlipDirection = false
  Size = 1
  Size2 = 1
  SupportTransform = false
  UseAllEdges = false
FEATURE [PartDesign::Body] Body011  label="couvercle_coiffe_V1"
  Group = -> [Sketch016,Pad010,Chamfer003,Sketch017,Pad011,Sketch018,Pad012,Sketch019,Pad013,Chamfer004]
  Origin = -> Origin011
  Placement = pos=(0,0,200.3) rot=(0,0,1;0rad)
  Tip = -> Chamfer004
FEATURE [Mesh::Feature] Mesh001  label="couvercle_coiffe_V1 (Meshed)"
FEATURE [Sketcher::SketchObject] Sketch020
  FullyConstrained = true
  MapMode = 5
  Support = -> [XY_Plane012]
  sketch-geometry (2):
    g0: Circle CenterX=0 CenterY=0 CenterZ=0 NormalX=0 NormalY=0 NormalZ=1 AngleXU=0 Radius=9.25
    g1: Circle CenterX=0 CenterY=0 CenterZ=0 NormalX=0 NormalY=0 NormalZ=1 AngleXU=0 Radius=11.75
  constraints (4):
    c: Coincident(g0,g-1)
    c: Coincident(g1,g0)
    c: Radius(g1) = 11.75
    c: Radius(g0) = 9.25
FEATURE [PartDesign::Pad] Pad014
  Direction = (1,1,1)
  Length = 70
  Length2 = 100
  Profile = -> Sketch020
  Type = 0
FEATURE [Sketcher::SketchObject] Sketch021
  FullyConstrained = true
  MapMode = 5
  Placement = pos=(0,0,0) rot=(1,0,0;3.14159rad)
  Support = -> [Pad014]
  sketch-geometry (4):
    g0: LineSegment StartX=-15.74 StartY=1.5 StartZ=0 EndX=15.74 EndY=1.5 EndZ=0
    g1: LineSegment StartX=15.74 StartY=1.5 StartZ=0 EndX=15.74 EndY=-1.5 EndZ=0
    g2: LineSegment StartX=15.74 StartY=-1.5 StartZ=0 EndX=-15.74 EndY=-1.5 EndZ=0
    g3: LineSegment StartX=-15.74 StartY=-1.5 StartZ=0 EndX=-15.74 EndY=1.5 EndZ=0
  constraints (11):
    c: Coincident(g0,g1)
    c: Coincident(g1,g2)
    c: Coincident(g2,g3)
    c: Coincident(g3,g0)
    c: Horizontal(g0)
    c: Horizontal(g2)
    c: Vertical(g1)
    c: Vertical(g3)
    c: Symmetric(g1,g0,g-1)
    c: DistanceX(g2,g2) = 31.48
    c: DistanceY(g1,g1) = 3
FEATURE [PartDesign::Pocket] Pocket004
  BaseFeature = -> Pad014
  Direction = (1,1,1)
  Length = 67
  Length2 = 100
  Profile = -> Sketch021
  Type = 0
FEATURE [PartDesign::Chamfer] Chamfer005
  Angle = 45
  Base = -> Pocket004 [Edge3,Edge7]
  BaseFeature = -> Pocket004
  ChamferType = 0
  FlipDirection = false
  Size = 2
  Size2 = 1
  SupportTransform = false
  UseAllEdges = false
FEATURE [Sketcher::SketchObject] Sketch022
  FullyConstrained = true
  MapMode = 5
  Placement = pos=(0,0,0) rot=(1,0,0;3.14159rad)
  Support = -> [Chamfer005]
  sketch-geometry (4):
    g0: LineSegment StartX=-1.5 StartY=15.795 StartZ=0 EndX=1.5 EndY=15.795 EndZ=0
    g1: LineSegment StartX=1.5 StartY=15.795 StartZ=0 EndX=1.5 EndY=-15.795 EndZ=0
    g2: LineSegment StartX=1.5 StartY=-15.795 StartZ=0 EndX=-1.5 EndY=-15.795 EndZ=0
    g3: LineSegment StartX=-1.5 StartY=-15.795 StartZ=0 EndX=-1.5 EndY=15.795 EndZ=0
  constraints (11):
    c: Coincident(g0,g1)
    c: Coincident(g1,g2)
    c: Coincident(g2,g3)
    c: Coincident(g3,g0)
    c: Horizontal(g0)
    c: Horizontal(g2)
    c: Vertical(g1)
    c: Vertical(g3)
    c: Symmetric(g1,g0,g-1)
    c: DistanceX(g2,g2) = 3
    c: DistanceY(g1,g1) = 31.59
FEATURE [PartDesign::Pocket] Pocket005
  BaseFeature = -> Chamfer005
  Direction = (1,1,1)
  Length = 67
  Length2 = 100
  Profile = -> Sketch022
  Type = 0
FEATURE [PartDesign::Body] Body012  label="Adaptateur_moteur_V1"
  Group = -> [Sketch020,Pad014,Sketch021,Pocket004,Chamfer005,Sketch022,Pocket005]
  Origin = -> Origin012
  Placement = pos=(0,8e-15,69) rot=(1,0,0;3.14159rad)
  Tip = -> Pocket005
FEATURE [Mesh::Feature] Mesh002  label="couvercle_coiffe_V1 (Meshed)001"
FEATURE [Sketcher::SketchObject] Sketch023
  FullyConstrained = true
  MapMode = 5
  Support = -> [XY_Plane013]
  sketch-geometry (2):
    g0: Circle CenterX=0 CenterY=0 CenterZ=0 NormalX=0 NormalY=0 NormalZ=1 AngleXU=0 Radius=9.25
    g1: Circle CenterX=0 CenterY=0 CenterZ=0 NormalX=0 NormalY=0 NormalZ=1 AngleXU=0 Radius=11.75
  constraints (4):
    c: Coincident(g0,g-1)
    c: Coincident(g1,g0)
    c: Radius(g1) = 11.75
    c: Radius(g0) = 9.25
FEATURE [PartDesign::Pad] Pad015
  Direction = (1,1,1)
  Length = 70
  Length2 = 100
  Profile = -> Sketch023
  Type = 0
FEATURE [Sketcher::SketchObject] Sketch025
  FullyConstrained = true
  MapMode = 5
  Placement = pos=(0,0,0) rot=(1,0,0;3.14159rad)
  Support = -> [Pad015]
  sketch-geometry (4):
    g0: LineSegment StartX=-15.74 StartY=1.5 StartZ=0 EndX=15.74 EndY=1.5 EndZ=0
    g1: LineSegment StartX=15.74 StartY=1.5 StartZ=0 EndX=15.74 EndY=-1.5 EndZ=0
    g2: LineSegment StartX=15.74 StartY=-1.5 StartZ=0 EndX=-15.74 EndY=-1.5 EndZ=0
    g3: LineSegment StartX=-15.74 StartY=-1.5 StartZ=0 EndX=-15.74 EndY=1.5 EndZ=0
  constraints (11):
    c: Coincident(g0,g1)
    c: Coincident(g1,g2)
    c: Coincident(g2,g3)
    c: Coincident(g3,g0)
    c: Horizontal(g0)
    c: Horizontal(g2)
    c: Vertical(g1)
    c: Vertical(g3)
    c: Symmetric(g1,g0,g-1)
    c: DistanceX(g2,g2) = 31.48
    c: DistanceY(g1,g1) = 3
FEATURE [PartDesign::Pocket] Pocket007
  BaseFeature = -> Pad015
  Direction = (1,1,1)
  Length = 67
  Length2 = 100
  Profile = -> Sketch025
  Type = 0
FEATURE [PartDesign::Chamfer] Chamfer006
  Angle = 45
  Base = -> Pocket007 [Edge3,Edge7]
  BaseFeature = -> Pocket007
  ChamferType = 0
  FlipDirection = false
  Size = 2
  Size2 = 1
  SupportTransform = false
  UseAllEdges = false
FEATURE [Sketcher::SketchObject] Sketch024
  ExternalGeometry = -> [Chamfer006]
  FullyConstrained = true
  MapMode = 5
  Placement = pos=(0,0,0) rot=(1,0,0;3.14159rad)
  Support = -> [Chamfer006]
  sketch-geometry (8):
    g0: LineSegment StartX=-1.5 StartY=13.94 StartZ=0 EndX=11.6539 EndY=13.94 EndZ=0
    g1: LineSegment StartX=11.6539 StartY=13.94 StartZ=0 EndX=11.6539 EndY=1.5 EndZ=0
    g2: LineSegment StartX=11.6539 StartY=1.5 StartZ=0 EndX=-1.5 EndY=1.5 EndZ=0
    g3: LineSegment StartX=-1.5 StartY=1.5 StartZ=0 EndX=-1.5 EndY=13.94 EndZ=0
    g4: LineSegment StartX=-11.6539 StartY=-1.5 StartZ=0 EndX=1.5 EndY=-1.5 EndZ=0
    g5: LineSegment StartX=1.5 StartY=-1.5 StartZ=0 EndX=1.5 EndY=-13.94 EndZ=0
    g6: LineSegment StartX=1.5 StartY=-13.94 StartZ=0 EndX=-11.6539 EndY=-13.94 EndZ=0
    g7: LineSegment StartX=-11.6539 StartY=-13.94 StartZ=0 EndX=-11.6539 EndY=-1.5 EndZ=0
  constraints (21):
    c: Coincident(g0,g1)
    c: Coincident(g1,g2)
    c: Coincident(g2,g3)
    c: Coincident(g3,g0)
    c: Horizontal(g0)
    c: Horizontal(g2)
    c: Vertical(g1)
    c: Vertical(g3)
    c: Coincident(g1,g-3)
    c: DistanceX(g-2,g0) = -1.5
    c: DistanceY(g1,g1) = 12.44
    c: Coincident(g4,g5)
    c: Coincident(g5,g6)
    c: Coincident(g6,g7)
    c: Coincident(g7,g4)
    c: Horizontal(g4)
    c: Horizontal(g6)
    c: Vertical(g5)
    c: Vertical(g7)
    c: Coincident(g4,g-4)
    c: Symmetric(g5,g0,g-1)
FEATURE [PartDesign::Pocket] Pocket006
  BaseFeature = -> Chamfer006
  Direction = (1,1,1)
  Length = 67
  Length2 = 100
  Profile = -> Sketch024
  Type = 0
FEATURE [PartDesign::Body] Body013  label="Adaptateur_moteur_V2"
  Group = -> [Sketch023,Pad015,Sketch025,Pocket007,Chamfer006,Sketch024,Pocket006]
  Origin = -> Origin013
  Placement = pos=(0,8e-15,69) rot=(1,0,0;3.14159rad)
  Tip = -> Pocket006
FEATURE [Sketcher::SketchObject] Sketch026
  FullyConstrained = true
  MapMode = 5
  Placement = pos=(0,0,0) rot=(0.57735,0.57735,0.57735;2.0944rad)
  Support = -> [YZ_Plane014]
  sketch-geometry (4):
    g0: LineSegment StartX=12.5 StartY=0 StartZ=0 EndX=-12.5 EndY=0 EndZ=0
    g1: LineSegment StartX=-12.5 StartY=0 StartZ=0 EndX=-12.5 EndY=80 EndZ=0
    g2: LineSegment StartX=-12.5 StartY=80 StartZ=0 EndX=12.5 EndY=80 EndZ=0
    g3: LineSegment StartX=12.5 StartY=80 StartZ=0 EndX=12.5 EndY=0 EndZ=0
  constraints (11):
    c: Coincident(g0,g1)
    c: Coincident(g1,g2)
    c: Coincident(g2,g3)
    c: Coincident(g3,g0)
    c: Horizontal(g0)
    c: Vertical(g1)
    c: Vertical(g3)
    c: PointOnObject(g0,g-1)
    c: Symmetric(g1,g2,g-2)
    c: DistanceX(g2,g2) = 25
    c: DistanceY(g3,g3) = 80
FEATURE [PartDesign::Pad] Pad016
  Direction = (1,1,1)
  Length = 27
  Length2 = 100
  Midplane = true
  Placement = pos=(0,0,0) rot=(0.57735,0.57735,0.57735;2.0944rad)
  Profile = -> Sketch026
  Type = 0
FEATURE [PartDesign::Body] Body014  label="Charge_utile_V1"
  Group = -> [Sketch026,Pad016]
  Origin = -> Origin014
  Placement = pos=(0,0,201) rot=(0,0,1;0rad)
  Tip = -> Pad016
FEATURE [Sketcher::SketchObject] Sketch027
  FullyConstrained = true
  MapMode = 5
  Support = -> [XY_Plane015]
  sketch-geometry (12):
    g0: LineSegment StartX=0 StartY=0 StartZ=0 EndX=134.73 EndY=0 EndZ=0
    g1: LineSegment StartX=134.73 StartY=-24 StartZ=0 EndX=134.73 EndY=0 EndZ=0
    g2: LineSegment StartX=134.73 StartY=-24 StartZ=0 EndX=120.272 EndY=-24 EndZ=0
    g3-g7: Circle x5 (B-spline internal-alignment scaffolding for g8; pole/knot coordinates omitted)
    g8: BSplineCurve PolesCount=5 KnotsCount=3 Degree=3 IsPeriodic=0
    g9: GeomPoint X=120.272 Y=-24 Z=0
    g10: GeomPoint X=62.1183 Y=-19.6849 Z=0
    g11: GeomPoint X=0 Y=0 Z=0
  constraints (23):
    c: Coincident(g0,g-1)
    c: PointOnObject(g0,g-1)
    c: Coincident(g1,g0)
    c: Vertical(g1)
    c: Coincident(g2,g1)
    c: Horizontal(g2)
    c: Coincident(g8,g2)
    c: Weight(g3) = 1
    c: Equal(g3, g4-g7) x4
    c: Coincident(g8,g0)
    c: InternalAlignment(g3-g7 -> g8) x5
    c: InternalAlignment(g9,g8)
    c: InternalAlignment(g10,g8)
    c: InternalAlignment(g11,g8)
    c: DistanceX(g6) = 33.4091
    c: DistanceY(g6) = -14.1378
    c: DistanceX(g5) = 61.0359
    c: DistanceY(g5) = -20.426
    c: DistanceX(g4) = 92.9923
    c: DistanceY(g4) = -23.75
    c: DistanceX(g2) = 120.272
    c: DistanceY(g2) = -24
    c: DistanceX(g0,g0) = 134.73
FEATURE [PartDesign::Revolution] Revolution002
  Angle = 360
  Axis = (1,0,0)
  Base = (0,0,0)
  Profile = -> Sketch027
  ReferenceAxis = -> X_Axis015
  Reversed = true
FEATURE [PartDesign::Thickness] Thickness001
  Base = -> Revolution002 [Face1]
  BaseFeature = -> Revolution002
  Intersection = false
  Join = 0
  Mode = 0
  SupportTransform = false
  Value = 1
FEATURE [Sketcher::SketchObject] Sketch028
  FullyConstrained = true
  MapMode = 5
  Placement = pos=(134.73,0,0) rot=(0.57735,0.57735,0.57735;2.0944rad)
  Support = -> [Thickness001]
  sketch-geometry (5):
    g0: Circle CenterX=1.1e-15 CenterY=0 CenterZ=0 NormalX=0 NormalY=0 NormalZ=1 AngleXU=0 Radius=25
    g1: ArcOfCircle CenterX=1.1e-15 CenterY=0 CenterZ=0 NormalX=0 NormalY=0 NormalZ=1 AngleXU=0 Radius=24 StartAngle=0.675132 EndAngle=2.46646
    g2: ArcOfCircle CenterX=1.1e-15 CenterY=0 CenterZ=0 NormalX=0 NormalY=0 NormalZ=1 AngleXU=0 Radius=24 StartAngle=3.81672 EndAngle=5.60805
    g3: LineSegment StartX=-18.735 StartY=15 StartZ=0 EndX=-18.735 EndY=-15 EndZ=0
    g4: LineSegment StartX=18.735 StartY=15 StartZ=0 EndX=18.735 EndY=-15 EndZ=0
  constraints (14):
    c: Coincident(g0,g-1)
    c: Radius(g0) = 25
    c: Coincident(g1,g0)
    c: Coincident(g2,g0)
    c: Symmetric(g2,g2,g-2)
    c: Symmetric(g2,g1,g-1)
    c: Radius(g1) = 24
    c: Equal(g1,g2)
    c: Coincident(g3,g1)
    c: Coincident(g3,g2)
    c: Coincident(g4,g1)
    c: Coincident(g4,g2)
    c: Symmetric(g1,g1,g-2)
    c: DistanceY(g4,g4) = 30
FEATURE [PartDesign::Pad] Pad017
  BaseFeature = -> Thickness001
  Direction = (1,1,1)
  Length = 10
  Length2 = 100
  Profile = -> Sketch028
  Reversed = true
  Type = 0
FEATURE [PartDesign::Chamfer] Chamfer007
  Angle = 45
  Base = -> Pad017 [Edge9,Edge6]
  BaseFeature = -> Pad017
  ChamferType = 0
  FlipDirection = false
  Size = 1
  Size2 = 1
  SupportTransform = false
  UseAllEdges = false
FEATURE [Sketcher::SketchObject] Sketch029
  FullyConstrained = true
  MapMode = 5
  Support = -> [XY_Plane016]
  sketch-geometry (8):
    g0: ArcOfCircle CenterX=0 CenterY=-2.3e-15 CenterZ=0 NormalX=0 NormalY=0 NormalZ=1 AngleXU=0 Radius=23.8 StartAngle=2.2259 EndAngle=4.05728
    g1: ArcOfCircle CenterX=0 CenterY=-2.3e-15 CenterZ=0 NormalX=0 NormalY=0 NormalZ=1 AngleXU=0 Radius=23.8 StartAngle=5.3675 EndAngle=7.19888
    g2: LineSegment StartX=-14.5 StartY=-18.873 StartZ=0 EndX=14.5 EndY=-18.873 EndZ=0
    g3: LineSegment StartX=-14.5 StartY=18.873 StartZ=0 EndX=14.5 EndY=18.873 EndZ=0
    g4: ArcOfCircle CenterX=0 CenterY=-2.3e-15 CenterZ=0 NormalX=0 NormalY=0 NormalZ=1 AngleXU=0 Radius=22.6 StartAngle=2.22941 EndAngle=4.05377
    g5: ArcOfCircle CenterX=0 CenterY=-2.3e-15 CenterZ=0 NormalX=0 NormalY=0 NormalZ=1 AngleXU=0 Radius=22.6 StartAngle=5.371 EndAngle=7.19537
    g6: LineSegment StartX=-13.8317 StartY=17.873 StartZ=0 EndX=13.8317 EndY=17.873 EndZ=0
    g7: LineSegment StartX=13.8317 StartY=-17.873 StartZ=0 EndX=-13.8317 EndY=-17.873 EndZ=0
  constraints (22):
    c: Coincident(g0,g-1)
    c: Coincident(g0,g1)
    c: Coincident(g0,g2)
    c: Coincident(g1,g2)
    c: Coincident(g1,g3)
    c: Coincident(g0,g3)
    c: Symmetric(g1,g0,g-2)
    c: Symmetric(g0,g1,g-2)
    c: Radius(g1) = 23.8
    c: Symmetric(g0,g0,g-1)
    c: DistanceX(g2,g2) = 29
    c: Coincident(g4,g0)
    c: Coincident(g5,g0)
    c: Coincident(g6,g4)
    c: Coincident(g6,g5)
    c: Coincident(g7,g5)
    c: Coincident(g7,g4)
    c: Symmetric(g5,g5,g-1)
    c: Symmetric(g5,g4,g-2)
    c: Radius(g5) = 22.6
    c: Horizontal(g7)
    c: Distance(g4,g3) = 1
FEATURE [PartDesign::Pad] Pad018
  Direction = (1,1,1)
  Length = 10
  Length2 = 100
  Profile = -> Sketch029
  Type = 0
FEATURE [PartDesign::Chamfer] Chamfer008
  Angle = 45
  Base = -> Pad018 [Edge7,Edge12]
  BaseFeature = -> Pad018
  ChamferType = 0
  FlipDirection = false
  Size = 0.5
  Size2 = 1
  SupportTransform = false
  UseAllEdges = false
FEATURE [Sketcher::SketchObject] Sketch030
  FullyConstrained = true
  MapMode = 5
  Placement = pos=(0,0,0) rot=(1,0,0;3.14159rad)
  Support = -> [Chamfer008]
  sketch-geometry (2):
    g0: Circle CenterX=0 CenterY=0 CenterZ=0 NormalX=0 NormalY=0 NormalZ=1 AngleXU=0 Radius=23.9
    g1: Circle CenterX=0 CenterY=0 CenterZ=0 NormalX=0 NormalY=0 NormalZ=1 AngleXU=0 Radius=22.6
  constraints (4):
    c: Coincident(g0,g-1)
    c: Radius(g0) = 23.9
    c: Coincident(g1,g0)
    c: Radius(g1) = 22.6
FEATURE [PartDesign::Pad] Pad019
  BaseFeature = -> Chamfer008
  Direction = (0,0,-1)
  Length = 24
  Length2 = 100
  Profile = -> Sketch030
  ReferenceAxis = -> Sketch030 [N_Axis]
  Type = 0
FEATURE [Sketcher::SketchObject] Sketch031
  ExternalGeometry = -> [Pad019]
  FullyConstrained = true
  MapMode = 5
  Placement = pos=(0,0,0) rot=(1,0,0;3.14159rad)
  Support = -> [Pad019]
  sketch-geometry (4):
    g0: ArcOfCircle CenterX=-1.1e-15 CenterY=0 CenterZ=0 NormalX=0 NormalY=0 NormalZ=1 AngleXU=0 Radius=23.9 StartAngle=3.98637 EndAngle=5.43841
    g1: ArcOfCircle CenterX=-1.1e-15 CenterY=0 CenterZ=0 NormalX=0 NormalY=0 NormalZ=1 AngleXU=0 Radius=23.9 StartAngle=0.844779 EndAngle=2.29681
    g2: LineSegment StartX=-15.8671 StartY=17.873 StartZ=0 EndX=15.8671 EndY=17.873 EndZ=0
    g3: LineSegment StartX=-15.8671 StartY=-17.873 StartZ=0 EndX=15.8671 EndY=-17.873 EndZ=0
  constraints (14):
    c: Coincident(g0,g-1)
    c: PointOnObject(g0,g-3)
    c: PointOnObject(g0,g-3)
    c: Coincident(g1,g0)
    c: PointOnObject(g1,g-3)
    c: PointOnObject(g1,g-3)
    c: Coincident(g2,g1)
    c: Coincident(g2,g1)
    c: Horizontal(g2)
    c: PointOnObject(g-4,g2)
    c: Coincident(g3,g0)
    c: Coincident(g3,g0)
    c: Horizontal(g3)
    c: PointOnObject(g-5,g3)
FEATURE [PartDesign::Pad] Pad020
  BaseFeature = -> Pad019
  Direction = (0,0,-1)
  Length = 2
  Length2 = 100
  Profile = -> Sketch031
  Type = 0
FEATURE [Sketcher::SketchObject] Sketch032
  ExternalGeometry = -> [Pad020]
  FullyConstrained = true
  MapMode = 5
  Placement = pos=(0,0,-24) rot=(1,0,0;3.14159rad)
  Support = -> [Pad020]
  sketch-geometry (3):
    g0: Circle CenterX=0 CenterY=0 CenterZ=0 NormalX=0 NormalY=0 NormalZ=1 AngleXU=0 Radius=23.9
    g1: Circle CenterX=-18 CenterY=3.5 CenterZ=0 NormalX=0 NormalY=0 NormalZ=1 AngleXU=0 Radius=1.5
    g2: Circle CenterX=-18 CenterY=-3.5 CenterZ=0 NormalX=0 NormalY=0 NormalZ=1 AngleXU=0 Radius=1.5
  constraints (8):
    c: Coincident(g0,g-1)
    c: Radius(g-3) = 23.9
    c: Radius(g0) = 23.9
    c: Radius(g2) = 1.5
    c: Equal(g2,g1)
    c: Symmetric(g1,g2,g-1)
    c: DistanceX(g-2,g1) = -18
    c: DistanceY(g-1,g1) = 3.5
FEATURE [PartDesign::Pad] Pad021
  BaseFeature = -> Pad020
  Direction = (0,0,-1)
  Length = 2
  Length2 = 100
  Profile = -> Sketch032
  Type = 0
FEATURE [Sketcher::SketchObject] Sketch033
  FullyConstrained = true
  MapMode = 5
  Placement = pos=(0,0,0) rot=(1,0,0;1.5708rad)
  Support = -> [XZ_Plane015]
  sketch-geometry (4):
    g0: LineSegment StartX=-0.5 StartY=0 StartZ=0 EndX=14.5 EndY=0 EndZ=0
    g1: LineSegment StartX=24.4481 StartY=10.14 StartZ=0 EndX=-0.5 EndY=0 EndZ=0
    g2: LineSegment StartX=24.4481 StartY=10.14 StartZ=0 EndX=34.6427 EndY=13.7353 EndZ=0
    g3: LineSegment StartX=34.6427 StartY=13.7353 StartZ=0 EndX=14.5 EndY=0 EndZ=0
  constraints (12):
    c: PointOnObject(g0,g-1)
    c: PointOnObject(g0,g-1)
    c: DistanceX(g0,g0) = 15
    c: DistanceX(g-2,g0) = -0.5
    c: Coincident(g1,g0)
    c: DistanceY(g0,g1) = 10.14
    c: Coincident(g1,g2)
    c: Coincident(g2,g3)
    c: Coincident(g3,g0)
    c: Distance(g3) = 24.38
    c: Distance(g2) = 10.81
    c: Distance(g1) = 26.93
FEATURE [PartDesign::Revolution] Revolution003
  Angle = 360
  Axis = (1,0,0)
  Base = (0,0,0)
  BaseFeature = -> Chamfer007
  Profile = -> Sketch033
  ReferenceAxis = -> Sketch033 [H_Axis]
FEATURE [Sketcher::SketchObject] Sketch034
  FullyConstrained = true
  MapMode = 5
  Placement = pos=(-2.3e-15,18.873,0) rot=(0,0.707107,0.707107;3.14159rad)
  Support = -> [Pad021]
  sketch-geometry (1):
    g0: Circle CenterX=0 CenterY=5 CenterZ=0 NormalX=0 NormalY=0 NormalZ=1 AngleXU=0 Radius=1.5
  constraints (3):
    c: PointOnObject(g0,g-2)
    c: DistanceY(g-1,g0) = 5
    c: Diameter(g0) = 3
FEATURE [PartDesign::Pocket] Pocket008
  BaseFeature = -> Pad021
  Direction = (1e-16,-1,2e-16)
  Length = 100
  Length2 = 5
  Profile = -> Sketch034
  ReferenceAxis = -> Sketch034 [N_Axis]
  Type = 0
FEATURE [PartDesign::Body] Body016  label="couvercle_coiffe_V002"
  Group = -> [Sketch029,Pad018,Chamfer008,Sketch030,Pad019,Sketch031,Pad020,Sketch032,Pad021,Sketch034,Pocket008]
  Origin = -> Origin016
  Placement = pos=(0,0,200.3) rot=(0,0,1;0rad)
  Tip = -> Pocket008
FEATURE [Sketcher::SketchObject] Sketch035
  ExternalGeometry = -> [Revolution003]
  FullyConstrained = true
  MapMode = 5
  Placement = pos=(0,0,0) rot=(1,0,0;1.5708rad)
  Support = -> [XZ_Plane015]
  sketch-geometry (1):
    g0: Circle CenterX=129.73 CenterY=0 CenterZ=0 NormalX=0 NormalY=0 NormalZ=1 AngleXU=0 Radius=1.5
  constraints (3):
    c: PointOnObject(g0,g-1)
    c: Diameter(g0) = 3
    c: Distance(g0,g-3) = 5
FEATURE [PartDesign::Pocket] Pocket009
  BaseFeature = -> Revolution003
  Direction = (0,1,2e-16)
  Length = 200
  Length2 = 5
  Midplane = true
  Profile = -> Sketch035
  ReferenceAxis = -> Sketch035 [N_Axis]
  Type = 0
FEATURE [Sketcher::SketchObject] Sketch036
  ExternalGeometry = -> [Pocket009]
  FullyConstrained = true
  MapMode = 5
  Placement = pos=(134.73,0,0) rot=(0.57735,0.57735,0.57735;2.0944rad)
  Support = -> [Pocket009]
  sketch-geometry (8):
    g0: LineSegment StartX=-24.6779 StartY=4 StartZ=0 EndX=-29.6779 EndY=4 EndZ=0
    g1: LineSegment StartX=-29.6779 StartY=4 StartZ=0 EndX=-29.6779 EndY=-4 EndZ=0
    g2: LineSegment StartX=-29.6779 StartY=-4 StartZ=0 EndX=-24.6779 EndY=-4 EndZ=0
    g3: LineSegment StartX=-24.6779 StartY=-4 StartZ=0 EndX=-24.6779 EndY=4 EndZ=0
    g4: LineSegment StartX=24.6779 StartY=4 StartZ=0 EndX=29.6779 EndY=4 EndZ=0
    g5: LineSegment StartX=29.6779 StartY=4 StartZ=0 EndX=29.6779 EndY=-4 EndZ=0
    g6: LineSegment StartX=29.6779 StartY=-4 StartZ=0 EndX=24.6779 EndY=-4 EndZ=0
    g7: LineSegment StartX=24.6779 StartY=-4 StartZ=0 EndX=24.6779 EndY=4 EndZ=0
  constraints (21):
    c: Coincident(g0,g1)
    c: Coincident(g1,g2)
    c: Coincident(g2,g3)
    c: Coincident(g3,g0)
    c: Horizontal(g0)
    c: Horizontal(g2)
    c: Vertical(g3)
    c: PointOnObject(g0,g-3)
    c: Coincident(g4,g5)
    c: Coincident(g5,g6)
    c: Coincident(g6,g7)
    c: Coincident(g7,g4)
    c: Horizontal(g6)
    c: Vertical(g7)
    c: PointOnObject(g4,g-3)
    c: Symmetric(g1,g0,g-1)
    c: DistanceY(g3,g3) = 8
    c: DistanceX(g0,g0) = 5
    c: Symmetric(g5,g1,g-2)
    c: Symmetric(g4,g0,g-2)
    c: Horizontal(g4)
FEATURE [PartDesign::Pocket] Pocket010
  BaseFeature = -> Pocket009
  Direction = (-1,0,0)
  Length = 10
  Length2 = 5
  Profile = -> Sketch036
  ReferenceAxis = -> Sketch036 [N_Axis]
  Type = 0
FEATURE [Sketcher::SketchObject] Sketch037
  ExternalGeometry = -> [Pocket010]
  FullyConstrained = true
  MapMode = 5
  Placement = pos=(0,-24.6779,0) rot=(1,0,0;1.5708rad)
  Support = -> [Pocket010]
  sketch-geometry (1):
    g0: Circle CenterX=129.73 CenterY=0 CenterZ=0 NormalX=0 NormalY=0 NormalZ=1 AngleXU=0 Radius=4
  constraints (2):
    c: Coincident(g0,g-3)
    c: Diameter(g0) = 8
FEATURE [PartDesign::Pocket] Pocket011
  BaseFeature = -> Pocket010
  Direction = (0,1,-2e-16)
  Length = 3
  Length2 = 5
  Profile = -> Sketch037
  ReferenceAxis = -> Sketch037 [N_Axis]
  Type = 0
FEATURE [Sketcher::SketchObject] Sketch038
  ExternalGeometry = -> [Pocket011]
  FullyConstrained = true
  MapMode = 5
  Placement = pos=(0,24.6779,0) rot=(0,0.707107,0.707107;3.14159rad)
  Support = -> [Pocket011]
  sketch-geometry (1):
    g0: Circle CenterX=-129.73 CenterY=0 CenterZ=0 NormalX=0 NormalY=0 NormalZ=1 AngleXU=0 Radius=4
  constraints (2):
    c: Coincident(g0,g-3)
    c: Diameter(g0) = 8
FEATURE [PartDesign::Pocket] Pocket012
  BaseFeature = -> Pocket011
  Direction = (0,-1,2e-16)
  Length = 3
  Length2 = 5
  Profile = -> Sketch038
  ReferenceAxis = -> Sketch038 [N_Axis]
  Type = 0
FEATURE [PartDesign::Body] Body015  label="coiffe_V002"
  Group = -> [Sketch027,Revolution002,Thickness001,Sketch028,Pad017,Chamfer007,Sketch033,Revolution003,Sketch035,Pocket009,Sketch036,Pocket010,Sketch037,Pocket011,Sketch038,Pocket012]
  Origin = -> Origin015
  Placement = pos=(-7.4e-14,0,335) rot=(0,1,0;1.5708rad)
  Tip = -> Pocket012
FEATURE [Sketcher::SketchObject] Sketch039  label="profil haut"
  FullyConstrained = true
  MapMode = 5
  Support = -> [XY_Plane017]
  sketch-geometry (8):
    g0: ArcOfCircle CenterX=0 CenterY=-2.3e-15 CenterZ=0 NormalX=0 NormalY=0 NormalZ=1 AngleXU=0 Radius=23.8 StartAngle=2.2259 EndAngle=4.05728
    g1: ArcOfCircle CenterX=0 CenterY=-2.3e-15 CenterZ=0 NormalX=0 NormalY=0 NormalZ=1 AngleXU=0 Radius=23.8 StartAngle=5.3675 EndAngle=7.19888
    g2: LineSegment StartX=-14.5 StartY=-18.873 StartZ=0 EndX=14.5 EndY=-18.873 EndZ=0
    g3: LineSegment StartX=-14.5 StartY=18.873 StartZ=0 EndX=14.5 EndY=18.873 EndZ=0
    g4: ArcOfCircle CenterX=0 CenterY=-2.3e-15 CenterZ=0 NormalX=0 NormalY=0 NormalZ=1 AngleXU=0 Radius=22.6 StartAngle=2.22941 EndAngle=4.05377
    g5: ArcOfCircle CenterX=0 CenterY=-2.3e-15 CenterZ=0 NormalX=0 NormalY=0 NormalZ=1 AngleXU=0 Radius=22.6 StartAngle=5.371 EndAngle=7.19537
    g6: LineSegment StartX=-13.8317 StartY=17.873 StartZ=0 EndX=13.8317 EndY=17.873 EndZ=0
    g7: LineSegment StartX=13.8317 StartY=-17.873 StartZ=0 EndX=-13.8317 EndY=-17.873 EndZ=0
  constraints (22):
    c: Coincident(g0,g-1)
    c: Coincident(g0,g1)
    c: Coincident(g0,g2)
    c: Coincident(g1,g2)
    c: Coincident(g1,g3)
    c: Coincident(g0,g3)
    c: Symmetric(g1,g0,g-2)
    c: Symmetric(g0,g1,g-2)
    c: Radius(g1) = 23.8
    c: Symmetric(g0,g0,g-1)
    c: DistanceX(g2,g2) = 29
    c: Coincident(g4,g0)
    c: Coincident(g5,g0)
    c: Coincident(g6,g4)
    c: Coincident(g6,g5)
    c: Coincident(g7,g5)
    c: Coincident(g7,g4)
    c: Symmetric(g5,g5,g-1)
    c: Symmetric(g5,g4,g-2)
    c: Radius(g5) = 22.6
    c: Horizontal(g7)
    c: Distance(g4,g3) = 1
FEATURE [PartDesign::Pad] Pad022  label="extrusion partie haute"
  Direction = (0,0,1)
  Length = 10
  Length2 = 100
  Profile = -> Sketch039
  Type = 0
FEATURE [PartDesign::Chamfer] Chamfer009
  Angle = 45
  Base = -> Pad022 [Edge7,Edge12]
  BaseFeature = -> Pad022
  ChamferType = 0
  FlipDirection = false
  Size = 0.5
  Size2 = 1
  SupportTransform = false
  UseAllEdges = false
FEATURE [Sketcher::SketchObject] Sketch040  label="profil bas"
  FullyConstrained = true
  MapMode = 5
  Placement = pos=(0,0,0) rot=(1,0,0;3.14159rad)
  Support = -> [Chamfer009]
  sketch-geometry (2):
    g0: Circle CenterX=0 CenterY=0 CenterZ=0 NormalX=0 NormalY=0 NormalZ=1 AngleXU=0 Radius=23.9
    g1: Circle CenterX=0 CenterY=0 CenterZ=0 NormalX=0 NormalY=0 NormalZ=1 AngleXU=0 Radius=22.6
  constraints (4):
    c: Coincident(g0,g-1)
    c: Radius(g0) = 23.9
    c: Coincident(g1,g0)
    c: Radius(g1) = 22.6
FEATURE [PartDesign::Pad] Pad023  label="extrusion partie basse"
  BaseFeature = -> Chamfer009
  Direction = (0,0,-1)
  Length = 24
  Length2 = 100
  Profile = -> Sketch040
  ReferenceAxis = -> Sketch040 [N_Axis]
  Type = 0
FEATURE [Sketcher::SketchObject] Sketch041
  ExternalGeometry = -> [Pad023]
  FullyConstrained = true
  MapMode = 5
  Support = -> [Pad023]
  sketch-geometry (26):
    g0: Circle CenterX=0 CenterY=-2.3e-15 CenterZ=0 NormalX=0 NormalY=0 NormalZ=1 AngleXU=0 Radius=23.5
    g1: LineSegment StartX=-22.4062 StartY=2.95326 StartZ=0 EndX=-17 EndY=2 EndZ=0
    g2: LineSegment StartX=-17 StartY=2 StartZ=0 EndX=-17 EndY=1 EndZ=0
    g3: LineSegment StartX=-17 StartY=-1 StartZ=0 EndX=-17 EndY=-2 EndZ=0
    g4: LineSegment StartX=-17 StartY=-2 StartZ=0 EndX=-22.4062 EndY=-2.95326 EndZ=0
    g5: LineSegment StartX=-17 StartY=-1 StartZ=0 EndX=-19 EndY=-1 EndZ=0
    g6: LineSegment StartX=-17 StartY=1 StartZ=0 EndX=-19 EndY=1 EndZ=0
    g7: LineSegment StartX=-19 StartY=1 StartZ=0 EndX=-19 EndY=-1 EndZ=0
    g8: GeomPoint X=-22.6 Y=0 Z=0
    g9: LineSegment StartX=19 StartY=1 StartZ=0 EndX=19 EndY=-1 EndZ=0
    g10: LineSegment StartX=19 StartY=-1 StartZ=0 EndX=17 EndY=-1 EndZ=0
    g11: LineSegment StartX=17 StartY=-1 StartZ=0 EndX=17 EndY=-2 EndZ=0
    g12: LineSegment StartX=17 StartY=-2 StartZ=0 EndX=22.4062 EndY=-2.95326 EndZ=0
    g13: LineSegment StartX=19 StartY=1 StartZ=0 EndX=17 EndY=1 EndZ=0
    g14: LineSegment StartX=17 StartY=1 StartZ=0 EndX=17 EndY=2 EndZ=0
    g15: LineSegment StartX=17 StartY=2 StartZ=0 EndX=22.4062 EndY=2.95326 EndZ=0
    g16: ArcOfCircle CenterX=0 CenterY=-2.3e-15 CenterZ=0 NormalX=0 NormalY=0 NormalZ=1 AngleXU=0 Radius=22.6 StartAngle=3.27264 EndAngle=3.55712
    g17: ArcOfCircle CenterX=0 CenterY=-2.3e-15 CenterZ=0 NormalX=0 NormalY=0 NormalZ=1 AngleXU=0 Radius=22.6 StartAngle=5.86766 EndAngle=6.15214
    g18: LineSegment StartX=-10 StartY=-17.873 StartZ=0 EndX=-10 EndY=-10.123 EndZ=0
    g19: LineSegment StartX=-10 StartY=-17.873 StartZ=0 EndX=10 EndY=-17.873 EndZ=0
    g20: LineSegment StartX=10 StartY=-17.873 StartZ=0 EndX=10 EndY=-10.123 EndZ=0
    g21: ArcOfCircle CenterX=0 CenterY=-2.3e-15 CenterZ=0 NormalX=0 NormalY=0 NormalZ=1 AngleXU=0 Radius=22.6 StartAngle=2.22941 EndAngle=3.01054
    g22: ArcOfCircle CenterX=0 CenterY=-2.3e-15 CenterZ=0 NormalX=0 NormalY=0 NormalZ=1 AngleXU=0 Radius=22.6 StartAngle=0.13105 EndAngle=0.912181
    g23: LineSegment StartX=13.8317 StartY=17.873 StartZ=0 EndX=-13.8317 EndY=17.873 EndZ=0
    g24: LineSegment StartX=-10 StartY=-10.123 StartZ=0 EndX=10 EndY=-10.123 EndZ=0
    g25: LineSegment StartX=-20.6768 StartY=-9.123 StartZ=0 EndX=20.6768 EndY=-9.123 EndZ=0
  constraints (66):
    c: Coincident(g0,g-3)
    c: Coincident(g1,g2)
    c: Vertical(g2)
    c: Coincident(g3,g4)
    c: Coincident(g3,g5)
    c: Symmetric(g2,g3,g-1)
    c: Distance(g3,g2) = 2
    c: Horizontal(g5)
    c: Coincident(g6,g2)
    c: Horizontal(g6)
    c: Coincident(g7,g6)
    c: Coincident(g7,g5)
    c: Symmetric(g1,g3,g-1)
    c: Angle(g1,g2) = 1.74533
    c: Symmetric(g1,g4,g-1)
    c: Vertical(g7)
    c: PointOnObject(g8,g-1)
    c: PointOnObject(g8,g-7)
    c: DistanceX(g6,g6) = 2
    c: DistanceY(g3,g3) = 1
    c: Coincident(g9,g10)
    c: Coincident(g10,g11)
    c: Coincident(g11,g12)
    c: Coincident(g9,g13)
    c: Coincident(g13,g14)
    c: Coincident(g14,g15)
    c: Symmetric(g9,g9,g-1)
    c: Symmetric(g11,g14,g-1)
    c: Vertical(g11)
    c: Vertical(g14)
    c: Horizontal(g13)
    c: Horizontal(g10)
    c: Symmetric(g9,g6,g-2)
    c: Symmetric(g14,g1,g-2)
    c: Symmetric(g1,g15,g-2)
    c: Symmetric(g15,g12,g-1)
    c: Coincident(g16,g0)
    c: Coincident(g16,g4)
    c: Coincident(g17,g0)
    c: Coincident(g17,g12)
    c: PointOnObject(g18,g-5)
    c: Vertical(g18)
    c: PointOnObject(g19,g18)
    c: PointOnObject(g19,g-5)
    c: Horizontal(g19)
    c: Coincident(g19,g20)
    c: Vertical(g20)
    c: Symmetric(g18,g20,g-2)
    c: Distance(g18,g20) = 20
    c: DistanceY(g20,g20) = 7.75
    c: Diameter(g0) = 47
    c: Coincident(g21,g0)
    c: Coincident(g21,g1)
    c: Coincident(g21,g-7)
    c: Coincident(g22,g0)
    c: Coincident(g22,g15)
    c: Coincident(g23,g22)
    c: Coincident(g23,g21)
    c: Horizontal(g23)
    c: Distance(g5,g9) = 38
    c: Coincident(g24,g18)
    c: Coincident(g24,g20)
    c: Coincident(g25,g16)
    c: Coincident(g25,g17)
    c: Horizontal(g25)
    c: Distance(g20,g25) = 1
FEATURE [PartDesign::Pad] Pad024
  BaseFeature = -> Pad023
  Direction = (0,0,1)
  Length = 24
  Length2 = 10
  Profile = -> Sketch041
  ReferenceAxis = -> Sketch041 [N_Axis]
  Reversed = true
  Type = 0
FEATURE [Sketcher::SketchObject] Sketch042
  ExternalGeometry = -> [Pad024]
  FullyConstrained = true
  MapMode = 5
  Placement = pos=(0,0,-24) rot=(1,0,0;3.14159rad)
  Support = -> [Pad024]
  sketch-geometry (2):
    g0: Circle CenterX=0 CenterY=0 CenterZ=0 NormalX=0 NormalY=0 NormalZ=1 AngleXU=0 Radius=23.9
    g1: GeomPoint X=0 Y=23.9 Z=0
  constraints (4):
    c: PointOnObject(g1,g-3)
    c: PointOnObject(g1,g0)
    c: Coincident(g0,g-3)
    c: PointOnObject(g1,g-2)
FEATURE [PartDesign::Pad] Pad025
  BaseFeature = -> Pad024
  Direction = (0,0,-1)
  Length = 4
  Length2 = 10
  Profile = -> Sketch042
  ReferenceAxis = -> Sketch042 [N_Axis]
  Type = 0
FEATURE [PartDesign::Chamfer] Chamfer010
  Angle = 45
  Base = -> Pad025 [Edge56]
  BaseFeature = -> Pad025
  ChamferType = 0
  FlipDirection = false
  Size = 0.5
  Size2 = 1
  SupportTransform = false
  UseAllEdges = false
FEATURE [Sketcher::SketchObject] Sketch043
  FullyConstrained = true
  MapMode = 5
  Placement = pos=(0,0,-28) rot=(1,0,0;3.14159rad)
  Support = -> [Chamfer010]
  sketch-geometry (4):
    g0: Circle CenterX=0 CenterY=0 CenterZ=0 NormalX=0 NormalY=0 NormalZ=1 AngleXU=0 Radius=20.2
    g1: Circle CenterX=-16.25 CenterY=11.9991 CenterZ=0 NormalX=0 NormalY=0 NormalZ=1 AngleXU=0 Radius=1.5
    g2: Circle CenterX=16.25 CenterY=11.9991 CenterZ=0 NormalX=0 NormalY=0 NormalZ=1 AngleXU=0 Radius=1.5
    g3: Circle CenterX=0 CenterY=-20.2 CenterZ=0 NormalX=0 NormalY=0 NormalZ=1 AngleXU=0 Radius=1.5
  constraints (10):
    c: Coincident(g0,g-1)
    c: PointOnObject(g1,g0)
    c: PointOnObject(g3,g0)
    c: Equal(g3,g2)
    c: Equal(g3,g1)
    c: Diameter(g3) = 3
    c: Symmetric(g1,g2,g-2)
    c: PointOnObject(g3,g-2)
    c: Diameter(g0) = 40.4
    c: Distance(g1,g2) = 32.5
FEATURE [PartDesign::Pocket] Pocket013
  BaseFeature = -> Chamfer010
  Direction = (0,0,1)
  Length = 15
  Length2 = 5
  Profile = -> Sketch043
  ReferenceAxis = -> Sketch043 [N_Axis]
  Type = 0
FEATURE [Sketcher::SketchObject] Sketch044
  FullyConstrained = true
  MapMode = 5
  Placement = pos=(4.7e-15,-18.873,0) rot=(1,0,0;1.5708rad)
  Support = -> [Pocket013]
  sketch-geometry (1):
    g0: Circle CenterX=0 CenterY=5 CenterZ=0 NormalX=0 NormalY=0 NormalZ=1 AngleXU=0 Radius=1
  constraints (3):
    c: PointOnObject(g0,g-2)
    c: Diameter(g0) = 2
    c: DistanceY(g-1,g0) = 5
FEATURE [PartDesign::Pocket] Pocket014
  BaseFeature = -> Pocket013
  Direction = (-3e-16,1,-2e-16)
  Length = 100
  Length2 = 5
  Profile = -> Sketch044
  ReferenceAxis = -> Sketch044 [N_Axis]
  Type = 0
FEATURE [Sketcher::SketchObject] Sketch045
  FullyConstrained = true
  MapMode = 5
  Support = -> [Pocket014]
  sketch-geometry (2):
    g0: Circle CenterX=12.5 CenterY=-15 CenterZ=0 NormalX=0 NormalY=0 NormalZ=1 AngleXU=0 Radius=1.25
    g1: Circle CenterX=-12.5 CenterY=-15 CenterZ=0 NormalX=0 NormalY=0 NormalZ=1 AngleXU=0 Radius=1.25
  constraints (5):
    c: Symmetric(g1,g0,g-2)
    c: Equal(g1,g0)
    c: Diameter(g1) = 2.5
    c: Distance(g1,g0) = 25
    c: DistanceY(g-1,g1) = -15
FEATURE [PartDesign::Pocket] Pocket015
  BaseFeature = -> Pocket014
  Direction = (0,0,-1)
  Length = 15
  Length2 = 5
  Profile = -> Sketch045
  ReferenceAxis = -> Sketch045 [N_Axis]
  Type = 0
FEATURE [PartDesign::Body] Body017  label="couvercle_coiffe_V003"
  Group = -> [Sketch039,Pad022,Chamfer009,Sketch040,Pad023,Sketch041,Pad024,Sketch042,Pad025,Chamfer010,Sketch043,Pocket013,Sketch044,Pocket014,Sketch045,Pocket015]
  Origin = -> Origin017
  Placement = pos=(0,0,200.3) rot=(0,0,1;0rad)
  Tip = -> Pocket015
FEATURE [Mesh::Feature] Mesh003  label="couvercle_coiffe_V003 (Meshed)"
FEATURE [Sketcher::SketchObject] Sketch046
  FullyConstrained = false
  MapMode = 5
  Support = -> [XY_Plane018]
  sketch-geometry (27):
    g0: Circle CenterX=6.27e-14 CenterY=0 CenterZ=0 NormalX=0 NormalY=0 NormalZ=1 AngleXU=0 Radius=21.5
    g1: LineSegment StartX=-21.3218 StartY=2.76206 StartZ=0 EndX=-17 EndY=2 EndZ=0
    g2: LineSegment StartX=-17 StartY=2 StartZ=0 EndX=-17 EndY=1 EndZ=0
    g3: LineSegment StartX=-17 StartY=1 StartZ=0 EndX=-19 EndY=1 EndZ=0
    g4: LineSegment StartX=-19 StartY=1 StartZ=0 EndX=-19 EndY=-1 EndZ=0
    g5: LineSegment StartX=-19 StartY=-1 StartZ=0 EndX=-17 EndY=-1 EndZ=0
    g6: LineSegment StartX=-17 StartY=-1 StartZ=0 EndX=-17 EndY=-2 EndZ=0
    g7: LineSegment StartX=13 StartY=-17.1245 StartZ=0 EndX=10 EndY=-17.1245 EndZ=0
    g8: LineSegment StartX=10 StartY=-17.1245 StartZ=0 EndX=10 EndY=-10.1245 EndZ=0
    g9: LineSegment StartX=10 StartY=-10.1245 StartZ=0 EndX=-10 EndY=-10.1245 EndZ=0
    g10: LineSegment StartX=-10 StartY=-10.1245 StartZ=0 EndX=-10 EndY=-17.1245 EndZ=0
    g11: LineSegment StartX=-10 StartY=-17.1245 StartZ=0 EndX=-13 EndY=-17.1245 EndZ=0
    g12: ArcOfCircle CenterX=-9e-16 CenterY=0 CenterZ=0 NormalX=0 NormalY=0 NormalZ=1 AngleXU=0 Radius=21.5 StartAngle=5.36172 EndAngle=6.41201
    g13: LineSegment StartX=19.35 StartY=-2.41436 StartZ=0 EndX=17 EndY=-2 EndZ=0
    g14: LineSegment StartX=17 StartY=-2 StartZ=0 EndX=17 EndY=-1 EndZ=0
    g15: LineSegment StartX=17 StartY=-1 StartZ=0 EndX=19 EndY=-1 EndZ=0
    g16: LineSegment StartX=19 StartY=-1 StartZ=0 EndX=19 EndY=1 EndZ=0
    g17: LineSegment StartX=19 StartY=1 StartZ=0 EndX=17 EndY=1 EndZ=0
    g18: LineSegment StartX=17 StartY=1 StartZ=0 EndX=17 EndY=2 EndZ=0
    g19: LineSegment StartX=17 StartY=2 StartZ=0 EndX=21.3218 EndY=2.76206 EndZ=0
    g20: ArcOfCircle CenterX=-1.1e-15 CenterY=0 CenterZ=0 NormalX=0 NormalY=0 NormalZ=1 AngleXU=0 Radius=19.5 StartAngle=5.79709 EndAngle=6.15905
    g21: LineSegment StartX=17.2412 StartY=-9.11 StartZ=0 EndX=-17.2412 EndY=-9.11 EndZ=0
    g22: ArcOfCircle CenterX=-9e-16 CenterY=0 CenterZ=0 NormalX=0 NormalY=0 NormalZ=1 AngleXU=0 Radius=19.5 StartAngle=3.26572 EndAngle=3.62769
    g23: LineSegment StartX=-19.35 StartY=-2.41436 StartZ=0 EndX=-17 EndY=-2 EndZ=0
    g24: Circle CenterX=-12.5 CenterY=-15 CenterZ=0 NormalX=0 NormalY=0 NormalZ=1 AngleXU=0 Radius=1.5
    g25: Circle CenterX=12.5 CenterY=-15 CenterZ=0 NormalX=0 NormalY=0 NormalZ=1 AngleXU=0 Radius=1.5
    g26: ArcOfCircle CenterX=-9e-16 CenterY=0 CenterZ=0 NormalX=0 NormalY=0 NormalZ=1 AngleXU=0 Radius=21.5 StartAngle=3.01277 EndAngle=4.06306
  constraints (67):
    c: Diameter(g0) = 43
    c: PointOnObject(g11,g0)
    c: Coincident(g1,g2)
    c: Coincident(g2,g3)
    c: Horizontal(g3)
    c: Coincident(g3,g4)
    c: Coincident(g4,g5)
    c: Horizontal(g5)
    c: Coincident(g5,g6)
    c: Vertical(g6)
    c: Symmetric(g5,g2,g-1)
    c: Vertical(g4)
    c: DistanceY(g4,g4) = 2
    c: DistanceX(g5,g5) = 2
    c: DistanceY(g6,g6) = 1
    c: Symmetric(g6,g1,g-1)
    c: DistanceX(g-2,g2) = -17
    c: Angle(g1,g2) = 1.74533
    c: Coincident(g7,g8)
    c: Vertical(g8)
    c: Coincident(g8,g9)
    c: Coincident(g9,g10)
    c: Coincident(g10,g11)
    c: Symmetric(g11,g7,g-2)
    c: Horizontal(g11)
    c: Horizontal(g7)
    c: Vertical(g10)
    c: DistanceX(g11,g11) = 3
    c: DistanceY(g10,g10) = 7
    c: DistanceX(g9,g9) = 20
    c: Symmetric(g9,g8,g-2)
    c: Coincident(g12,g7)
    c: PointOnObject(g12,g0)
    c: Coincident(g13,g14)
    c: Vertical(g14)
    c: Coincident(g14,g15)
    c: Coincident(g15,g16)
    c: Coincident(g16,g17)
    c: Horizontal(g17)
    c: Coincident(g17,g18)
    c: Coincident(g18,g19)
    c: Coincident(g19,g12)
    c: Symmetric(g1,g18,g-2)
    c: Symmetric(g16,g3,g-2)
    c: Vertical(g18)
    c: Angle(g18,g19) = 1.74533
    c: Symmetric(g15,g4,g-2)
    c: Horizontal(g15)
    c: Angle(g13,g14) = 1.74533
    c: Symmetric(g6,g13,g-2)
    c: Coincident(g20,g13)
    c: Coincident(g21,g20)
    c: Radius(g20) = 19.5
    c: DistanceY(g-1,g20) = -9.11
    c: Coincident(g22,g21)
    c: Symmetric(g21,g20,g-2)
    c: Coincident(g23,g22)
    c: Coincident(g23,g6)
    c: Angle(g6,g23) = 1.74533
    c: Equal(g25,g24)
    c: Diameter(g25) = 3
    c: Symmetric(g24,g25,g-2)
    c: DistanceX(g-2,g24) = -12.5
    c: DistanceY(g-1,g24) = -15
    c: Coincident(g26,g12)
    c: Coincident(g26,g1)
    c: Coincident(g26,g11)
FEATURE [PartDesign::Pad] Pad026
  Direction = (0,0,1)
  Length = 32
  Length2 = 10
  Profile = -> Sketch046
  ReferenceAxis = -> Sketch046 [N_Axis]
  Type = 0
FEATURE [Sketcher::SketchObject] Sketch047
  ExternalGeometry = -> [Pad026]
  FullyConstrained = true
  MapMode = 5
  Placement = pos=(0,0,32) rot=(0,0,1;0rad)
  Support = -> [Pad026]
  sketch-geometry (4):
    g0: ArcOfCircle CenterX=-9e-16 CenterY=0 CenterZ=0 NormalX=0 NormalY=0 NormalZ=1 AngleXU=0 Radius=21.5 StartAngle=3.63191 EndAngle=4.06306
    g1: ArcOfCircle CenterX=-9e-16 CenterY=0 CenterZ=0 NormalX=0 NormalY=0 NormalZ=1 AngleXU=0 Radius=21.5 StartAngle=5.36172 EndAngle=5.79286
    g2: LineSegment StartX=-18.9669 StartY=-10.1245 StartZ=0 EndX=18.9669 EndY=-10.1245 EndZ=0
    g3: LineSegment StartX=-13 StartY=-17.1245 StartZ=0 EndX=13 EndY=-17.1245 EndZ=0
  constraints (10):
    c: Coincident(g0,g-4)
    c: Coincident(g0,g-3)
    c: Coincident(g1,g0)
    c: Coincident(g1,g-4)
    c: Coincident(g2,g0)
    c: Coincident(g2,g1)
    c: Horizontal(g2)
    c: PointOnObject(g-5,g2)
    c: Coincident(g3,g0)
    c: Coincident(g3,g1)
FEATURE [PartDesign::Pocket] Pocket016
  BaseFeature = -> Pad026
  Direction = (0,0,-1)
  Length = 21
  Length2 = 5
  Profile = -> Sketch047
  ReferenceAxis = -> Sketch047 [N_Axis]
  Type = 0
FEATURE [Sketcher::SketchObject] Sketch048
  ExternalGeometry = -> [Pocket016]
  FullyConstrained = true
  MapMode = 5
  Placement = pos=(0,0,32) rot=(0,0,1;0rad)
  Support = -> [Pocket016]
  sketch-geometry (8):
    g0: ArcOfCircle CenterX=-9e-16 CenterY=0 CenterZ=0 NormalX=0 NormalY=0 NormalZ=1 AngleXU=0 Radius=21.5 StartAngle=3.07177 EndAngle=3.63191
    g1: ArcOfCircle CenterX=-9e-16 CenterY=0 CenterZ=0 NormalX=0 NormalY=0 NormalZ=1 AngleXU=0 Radius=21.5 StartAngle=5.79286 EndAngle=6.35301
    g2: LineSegment StartX=-21.4476 StartY=1.5 StartZ=0 EndX=21.4476 EndY=1.5 EndZ=0
    g3: LineSegment StartX=6 StartY=-17.1245 StartZ=0 EndX=-6 EndY=-17.1245 EndZ=0
    g4: LineSegment StartX=-6 StartY=-17.1245 StartZ=0 EndX=-13 EndY=-10.1245 EndZ=0
    g5: LineSegment StartX=-13 StartY=-10.1245 StartZ=0 EndX=-18.9669 EndY=-10.1245 EndZ=0
    g6: LineSegment StartX=6 StartY=-17.1245 StartZ=0 EndX=13 EndY=-10.1245 EndZ=0
    g7: LineSegment StartX=13 StartY=-10.1245 StartZ=0 EndX=18.9669 EndY=-10.1245 EndZ=0
  constraints (20):
    c: Coincident(g0,g-3)
    c: Coincident(g0,g-4)
    c: Coincident(g1,g0)
    c: Coincident(g2,g0)
    c: Coincident(g2,g1)
    c: Horizontal(g2)
    c: Coincident(g3,g4)
    c: Coincident(g4,g5)
    c: Coincident(g5,g0)
    c: Horizontal(g5)
    c: Coincident(g3,g6)
    c: Coincident(g6,g7)
    c: Coincident(g7,g1)
    c: Symmetric(g6,g4,g-2)
    c: Angle(g6) = 0.785398
    c: Symmetric(g3,g3,g-2)
    c: Distance(g3,g7) = 7
    c: DistanceX(g3,g3) = 12
    c: Symmetric(g1,g0,g-2)
    c: DistanceY(g-1,g1) = 1.5
FEATURE [Sketcher::SketchObject] Sketch049
  ExternalGeometry = -> [Pocket016]
  FullyConstrained = true
  MapMode = 5
  Placement = pos=(0,0,32) rot=(0,0,1;0rad)
  Support = -> [Pocket016]
  sketch-geometry (4):
    g0: LineSegment StartX=-19.35 StartY=-2.41436 StartZ=0 EndX=19.35 EndY=-2.41436 EndZ=0
    g1: LineSegment StartX=19.35 StartY=-2.41436 StartZ=0 EndX=19.35 EndY=5.58564 EndZ=0
    g2: LineSegment StartX=19.35 StartY=5.58564 StartZ=0 EndX=-19.35 EndY=5.58564 EndZ=0
    g3: LineSegment StartX=-19.35 StartY=5.58564 StartZ=0 EndX=-19.35 EndY=-2.41436 EndZ=0
  constraints (10):
    c: Coincident(g0,g1)
    c: Coincident(g1,g2)
    c: Coincident(g2,g3)
    c: Coincident(g3,g0)
    c: Horizontal(g2)
    c: Vertical(g1)
    c: Vertical(g3)
    c: Coincident(g0,g-3)
    c: Symmetric(g0,g0,g-2)
    c: DistanceY(g3,g3) = 8
FEATURE [PartDesign::Pocket] Pocket017
  BaseFeature = -> Pocket016
  Direction = (0,0,-1)
  Length = 50
  Length2 = 5
  Profile = -> Sketch049
  ReferenceAxis = -> Sketch049 [N_Axis]
  Type = 0
FEATURE [PartDesign::Pad] Pad027
  BaseFeature = -> Pocket017
  Direction = (0,0,1)
  Length = 3
  Length2 = 10
  Profile = -> Sketch048
  ReferenceAxis = -> Sketch048 [N_Axis]
  Type = 0
FEATURE [Sketcher::SketchObject] Sketch050
  ExternalGeometry = -> [Pad027]
  FullyConstrained = true
  MapMode = 5
  Placement = pos=(0,0,32) rot=(0,0,1;0rad)
  Support = -> [Pad027]
  sketch-geometry (4):
    g0: LineSegment StartX=21.4476 StartY=1.5 StartZ=0 EndX=-21.4476 EndY=1.5 EndZ=0
    g1: LineSegment StartX=-21.4476 StartY=1.5 StartZ=0 EndX=-21.4476 EndY=9.5 EndZ=0
    g2: LineSegment StartX=-21.4476 StartY=9.5 StartZ=0 EndX=21.4476 EndY=9.5 EndZ=0
    g3: LineSegment StartX=21.4476 StartY=9.5 StartZ=0 EndX=21.4476 EndY=1.5 EndZ=0
  constraints (10):
    c: Coincident(g0,g1)
    c: Coincident(g1,g2)
    c: Coincident(g2,g3)
    c: Coincident(g3,g0)
    c: Horizontal(g2)
    c: Vertical(g1)
    c: Vertical(g3)
    c: Coincident(g0,g-3)
    c: Symmetric(g0,g0,g-2)
    c: DistanceY(g1,g1) = 8
FEATURE [PartDesign::Pocket] Pocket018
  BaseFeature = -> Pad027
  Direction = (0,0,-1)
  Length = 32
  Length2 = 5
  Profile = -> Sketch050
  ReferenceAxis = -> Sketch050 [N_Axis]
  Type = 0
FEATURE [Mesh::Feature] Mesh004  label="FixationLaMulog (Meshed)"
FEATURE [Sketcher::SketchObject] Sketch051
  FullyConstrained = true
  MapMode = 5
  Placement = pos=(0,0,35) rot=(0,0,1;0rad)
  Support = -> [Pocket018]
  sketch-geometry (1):
    g0: Circle CenterX=0 CenterY=0 CenterZ=0 NormalX=0 NormalY=0 NormalZ=1 AngleXU=0 Radius=23.5
  constraints (2):
    c: Coincident(g0,g-1)
    c: Diameter(g0) = 47
FEATURE [PartDesign::Pad] Pad028
  BaseFeature = -> Pocket018
  Direction = (0,0,1)
  Length = 1
  Length2 = 10
  Profile = -> Sketch051
  ReferenceAxis = -> Sketch051 [N_Axis]
  Type = 0
FEATURE [PartDesign::Body] Body018  label="FixationLaMulog"
  Group = -> [Sketch046,Pad026,Sketch047,Pocket016,Sketch048,Sketch049,Pocket017,Pad027,Sketch050,Pocket018,Sketch051,Pad028]
  Origin = -> Origin018
  Placement = pos=(0,0,200) rot=(0,0,1;0rad)
  Tip = -> Pad028
